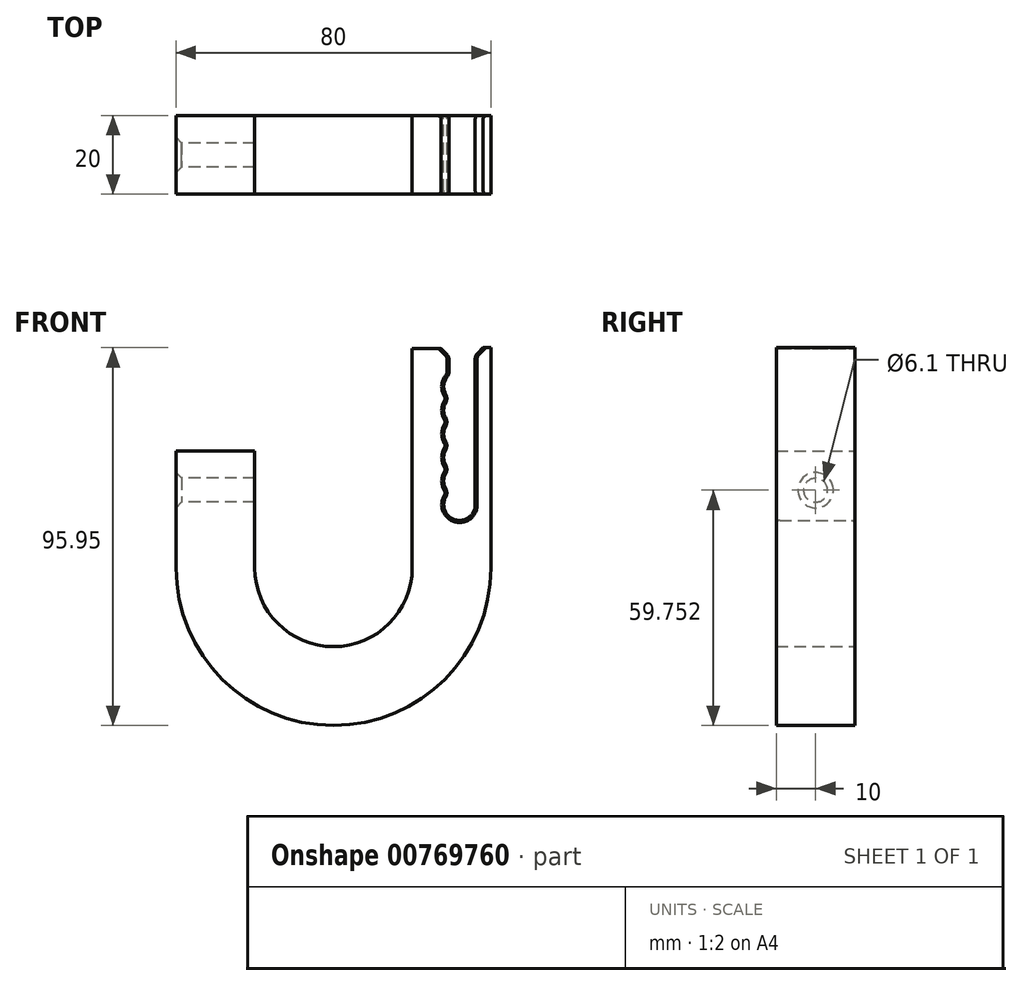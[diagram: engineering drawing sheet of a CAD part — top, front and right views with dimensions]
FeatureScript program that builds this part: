
annotation { "Feature Type Name" : "Feature", "Feature Type Description" : "" }
export const myFeature = defineFeature(function(context is Context, id is Id, definition is map)
    precondition{}
    {
        {
            var Q0;
            Q0=qCreatedBy(makeId("Front.planeOp"),FACE);
            var sketch = newSketch(context, id + "F0", { "sketchPlane" : qUnion([Q0])});
            skArc(sketch, "E0", {"start": v(0.07, 3) * mm, "mid": v(1.07, -3.65) * mm, "end": v(6.72, 0) * mm});
            skArc(sketch, "E1", {"start": v(0.07, 9) * mm, "mid": v(-1.28, 6) * mm, "end": v(0.07, 3) * mm});
            skArc(sketch, "E2", {"start": v(0.07, 15) * mm, "mid": v(-1.28, 12) * mm, "end": v(0.07, 9) * mm});
            skArc(sketch, "E3", {"start": v(0.07, 21) * mm, "mid": v(-1.28, 18) * mm, "end": v(0.07, 15) * mm});
            skArc(sketch, "E4", {"start": v(0.07, 27) * mm, "mid": v(-1.28, 24) * mm, "end": v(0.07, 21) * mm});
            skArc(sketch, "E5", {"start": v(0.07, 33) * mm, "mid": v(-1.28, 30) * mm, "end": v(0.07, 27) * mm});
            skLineSegment(sketch, "E6", {"start": v(6.72, 30) * mm, "end": v(6.72, 0) * mm});
            skLineSegment(sketch, "E7", {"start": v(0.07, 39.67) * mm, "end": v(-9.28, 39.67) * mm});
            skLineSegment(sketch, "E8", {"start": v(-9.28, 39.67) * mm, "end": v(-9.28, -16.06) * mm});
            skLineSegment(sketch, "E9", {"start": v(10.72, -16.06) * mm, "end": v(10.72, 39.9) * mm});
            skLineSegment(sketch, "E10", {"start": v(10.72, 39.9) * mm, "end": v(6.72, 39.9) * mm});
            skLineSegment(sketch, "E11", {"start": v(6.72, 39.9) * mm, "end": v(6.72, 30) * mm});
            skLineSegment(sketch, "E12", {"start": v(0.07, 33) * mm, "end": v(0.07, 39.67) * mm});
            skArc(sketch, "E13", {"start": v(-9.28, -16.06) * mm, "mid": v(-29.28, -36.06) * mm, "end": v(-49.28, -16.06) * mm});
            skArc(sketch, "E14", {"start": v(10.72, -16.06) * mm, "mid": v(-29.28, -56.06) * mm, "end": v(-69.28, -16.06) * mm});
            skLineSegment(sketch, "E15", {"start": v(-69.28, -16.06) * mm, "end": v(-69.28, 13.7) * mm});
            skLineSegment(sketch, "E16", {"start": v(-69.28, 13.7) * mm, "end": v(-49.28, 13.7) * mm});
            skLineSegment(sketch, "E17", {"start": v(-49.28, 13.7) * mm, "end": v(-49.28, -16.06) * mm});
            skSolve(sketch);
        }
        {
            var Q0;
            Q0 = qSketchRegion(id + "F0", true);
            extrude(context, id + "F1", {"entities" : qUnion([Q0]), "endBound" : BoundingType.SYMMETRIC, "depth" : 20 * mm, "offsetDistance" : 25 * mm});
        }
        {
            var Q0;
            Q0=makeQuery(id+"F1.opExtrude","SWEPT_EDGE",EDGE,{"disambiguationData":[OSD([sQuery(id+"F0.wireOp",EDGE,"E7"),sQuery(id+"F0.wireOp",EDGE,"E12")])]});
            var Q1;
            Q1=makeQuery(id+"F1.opExtrude","SWEPT_EDGE",EDGE,{"disambiguationData":[OSD([sQuery(id+"F0.wireOp",EDGE,"E10"),sQuery(id+"F0.wireOp",EDGE,"E11")])]});
            chamfer(context, id + "F2", {"entities" : qUnion([Q0, Q1]), "width" : 2 * mm, "tangentPropagation" : true});
        }
        {
            var Q0;
            {var subQ0=sQuery(id+"F0.wireOp",EDGE,"E12");Q0=makeQuery(id+"F2.opChamfer","BLEND_EDGE",EDGE,{"blendedFrom":[makeQuery(id+"F1.opExtrude","SWEPT_EDGE",EDGE,{"disambiguationData":[OSD([sQuery(id+"F0.wireOp",EDGE,"E7"),subQ0])]}),makeQuery(id+"F1.opExtrude","SWEPT_FACE",FACE,{"disambiguationData":[OSD([subQ0])]})],"blendedInto":[makeQuery(id+"F1.opExtrude","SWEPT_FACE",FACE,{"disambiguationData":[OSD([subQ0])]})]});}
            var Q1;
            Q1=makeQuery(id+"F1.opExtrude","SWEPT_EDGE",EDGE,{"disambiguationData":[OSD([sQuery(id+"F0.wireOp",EDGE,"E5"),sQuery(id+"F0.wireOp",EDGE,"E12")])]});
            var Q2;
            Q2=makeQuery(id+"F1.opExtrude","SWEPT_EDGE",EDGE,{"disambiguationData":[OSD([sQuery(id+"F0.wireOp",EDGE,"E4"),sQuery(id+"F0.wireOp",EDGE,"E5")])]});
            var Q3;
            Q3=makeQuery(id+"F1.opExtrude","SWEPT_EDGE",EDGE,{"disambiguationData":[OSD([sQuery(id+"F0.wireOp",EDGE,"E3"),sQuery(id+"F0.wireOp",EDGE,"E4")])]});
            var Q4;
            Q4=makeQuery(id+"F1.opExtrude","SWEPT_EDGE",EDGE,{"disambiguationData":[OSD([sQuery(id+"F0.wireOp",EDGE,"E2"),sQuery(id+"F0.wireOp",EDGE,"E3")])]});
            var Q5;
            Q5=makeQuery(id+"F1.opExtrude","SWEPT_EDGE",EDGE,{"disambiguationData":[OSD([sQuery(id+"F0.wireOp",EDGE,"E1"),sQuery(id+"F0.wireOp",EDGE,"E2")])]});
            var Q6;
            Q6=makeQuery(id+"F1.opExtrude","SWEPT_EDGE",EDGE,{"disambiguationData":[OSD([sQuery(id+"F0.wireOp",EDGE,"E0"),sQuery(id+"F0.wireOp",EDGE,"E1")])]});
            var Q7;
            {var subQ0=sQuery(id+"F0.wireOp",EDGE,"E11");Q7=makeQuery(id+"F2.opChamfer","BLEND_EDGE",EDGE,{"blendedFrom":[makeQuery(id+"F1.opExtrude","SWEPT_EDGE",EDGE,{"disambiguationData":[OSD([sQuery(id+"F0.wireOp",EDGE,"E10"),subQ0])]}),makeQuery(id+"F1.opExtrude","SWEPT_FACE",FACE,{"disambiguationData":[OSD([sQuery(id+"F0.wireOp",EDGE,"E6"),subQ0])]})],"blendedInto":[makeQuery(id+"F1.opExtrude","SWEPT_FACE",FACE,{"disambiguationData":[OSD([sQuery(id+"F0.wireOp",EDGE,"E6"),subQ0])]})]});}
            fillet(context, id + "F3", {"entities" : qUnion([Q0, Q1, Q2, Q3, Q4, Q5, Q6, Q7]), "radius" : 2 * mm, "tangentPropagation" : true, "allowEdgeOverflow" : false});
        }
        {
            var Q0;
            Q0=makeQuery(id+"F1.opExtrude","CAP_EDGE",EDGE,{"disambiguationData":[OSD([sQuery(id+"F0.wireOp",EDGE,"E5")])],"isStart":false});
            var Q1;
            {var subQ0=sQuery(id+"F0.wireOp",EDGE,"E5");var subQ1=sQuery(id+"F0.wireOp",EDGE,"E4");Q1=makeQuery(id+"F3.opFillet","BLEND_EDGE",EDGE,{"blendedFrom":[makeQuery(id+"F1.opExtrude","SWEPT_EDGE",EDGE,{"disambiguationData":[OSD([subQ1,subQ0])]}),makeQuery(id+"F1.opExtrude","CAP_FACE",FACE,{"disambiguationData":[OSD([sQuery(id+"F0.wireOp",EDGE,"E0"),sQuery(id+"F0.wireOp",EDGE,"E1"),sQuery(id+"F0.wireOp",EDGE,"E2"),sQuery(id+"F0.wireOp",EDGE,"E3"),subQ1,subQ0,sQuery(id+"F0.wireOp",EDGE,"E6"),sQuery(id+"F0.wireOp",EDGE,"E7"),sQuery(id+"F0.wireOp",EDGE,"E8"),sQuery(id+"F0.wireOp",EDGE,"E9"),sQuery(id+"F0.wireOp",EDGE,"E10"),sQuery(id+"F0.wireOp",EDGE,"E11"),sQuery(id+"F0.wireOp",EDGE,"E12"),sQuery(id+"F0.wireOp",EDGE,"E13"),sQuery(id+"F0.wireOp",EDGE,"E14"),sQuery(id+"F0.wireOp",EDGE,"E15"),sQuery(id+"F0.wireOp",EDGE,"E16"),sQuery(id+"F0.wireOp",EDGE,"E17")])],"isStart":false})],"blendedInto":[makeQuery(id+"F1.opExtrude","CAP_FACE",FACE,{"disambiguationData":[OSD([sQuery(id+"F0.wireOp",EDGE,"E0"),sQuery(id+"F0.wireOp",EDGE,"E1"),sQuery(id+"F0.wireOp",EDGE,"E2"),sQuery(id+"F0.wireOp",EDGE,"E3"),subQ1,subQ0,sQuery(id+"F0.wireOp",EDGE,"E6"),sQuery(id+"F0.wireOp",EDGE,"E7"),sQuery(id+"F0.wireOp",EDGE,"E8"),sQuery(id+"F0.wireOp",EDGE,"E9"),sQuery(id+"F0.wireOp",EDGE,"E10"),sQuery(id+"F0.wireOp",EDGE,"E11"),sQuery(id+"F0.wireOp",EDGE,"E12"),sQuery(id+"F0.wireOp",EDGE,"E13"),sQuery(id+"F0.wireOp",EDGE,"E14"),sQuery(id+"F0.wireOp",EDGE,"E15"),sQuery(id+"F0.wireOp",EDGE,"E16"),sQuery(id+"F0.wireOp",EDGE,"E17")])],"isStart":false})]});}
            var Q2;
            Q2=makeQuery(id+"F1.opExtrude","CAP_EDGE",EDGE,{"disambiguationData":[OSD([sQuery(id+"F0.wireOp",EDGE,"E4")])],"isStart":false});
            var Q3;
            {var subQ0=sQuery(id+"F0.wireOp",EDGE,"E4");var subQ1=sQuery(id+"F0.wireOp",EDGE,"E3");Q3=makeQuery(id+"F3.opFillet","BLEND_EDGE",EDGE,{"blendedFrom":[makeQuery(id+"F1.opExtrude","SWEPT_EDGE",EDGE,{"disambiguationData":[OSD([subQ1,subQ0])]}),makeQuery(id+"F1.opExtrude","CAP_FACE",FACE,{"disambiguationData":[OSD([sQuery(id+"F0.wireOp",EDGE,"E0"),sQuery(id+"F0.wireOp",EDGE,"E1"),sQuery(id+"F0.wireOp",EDGE,"E2"),subQ1,subQ0,sQuery(id+"F0.wireOp",EDGE,"E5"),sQuery(id+"F0.wireOp",EDGE,"E6"),sQuery(id+"F0.wireOp",EDGE,"E7"),sQuery(id+"F0.wireOp",EDGE,"E8"),sQuery(id+"F0.wireOp",EDGE,"E9"),sQuery(id+"F0.wireOp",EDGE,"E10"),sQuery(id+"F0.wireOp",EDGE,"E11"),sQuery(id+"F0.wireOp",EDGE,"E12"),sQuery(id+"F0.wireOp",EDGE,"E13"),sQuery(id+"F0.wireOp",EDGE,"E14"),sQuery(id+"F0.wireOp",EDGE,"E15"),sQuery(id+"F0.wireOp",EDGE,"E16"),sQuery(id+"F0.wireOp",EDGE,"E17")])],"isStart":false})],"blendedInto":[makeQuery(id+"F1.opExtrude","CAP_FACE",FACE,{"disambiguationData":[OSD([sQuery(id+"F0.wireOp",EDGE,"E0"),sQuery(id+"F0.wireOp",EDGE,"E1"),sQuery(id+"F0.wireOp",EDGE,"E2"),subQ1,subQ0,sQuery(id+"F0.wireOp",EDGE,"E5"),sQuery(id+"F0.wireOp",EDGE,"E6"),sQuery(id+"F0.wireOp",EDGE,"E7"),sQuery(id+"F0.wireOp",EDGE,"E8"),sQuery(id+"F0.wireOp",EDGE,"E9"),sQuery(id+"F0.wireOp",EDGE,"E10"),sQuery(id+"F0.wireOp",EDGE,"E11"),sQuery(id+"F0.wireOp",EDGE,"E12"),sQuery(id+"F0.wireOp",EDGE,"E13"),sQuery(id+"F0.wireOp",EDGE,"E14"),sQuery(id+"F0.wireOp",EDGE,"E15"),sQuery(id+"F0.wireOp",EDGE,"E16"),sQuery(id+"F0.wireOp",EDGE,"E17")])],"isStart":false})]});}
            var Q4;
            Q4=makeQuery(id+"F1.opExtrude","CAP_EDGE",EDGE,{"disambiguationData":[OSD([sQuery(id+"F0.wireOp",EDGE,"E3")])],"isStart":false});
            var Q5;
            {var subQ0=sQuery(id+"F0.wireOp",EDGE,"E3");var subQ1=sQuery(id+"F0.wireOp",EDGE,"E2");Q5=makeQuery(id+"F3.opFillet","BLEND_EDGE",EDGE,{"blendedFrom":[makeQuery(id+"F1.opExtrude","SWEPT_EDGE",EDGE,{"disambiguationData":[OSD([subQ1,subQ0])]}),makeQuery(id+"F1.opExtrude","CAP_FACE",FACE,{"disambiguationData":[OSD([sQuery(id+"F0.wireOp",EDGE,"E0"),sQuery(id+"F0.wireOp",EDGE,"E1"),subQ1,subQ0,sQuery(id+"F0.wireOp",EDGE,"E4"),sQuery(id+"F0.wireOp",EDGE,"E5"),sQuery(id+"F0.wireOp",EDGE,"E6"),sQuery(id+"F0.wireOp",EDGE,"E7"),sQuery(id+"F0.wireOp",EDGE,"E8"),sQuery(id+"F0.wireOp",EDGE,"E9"),sQuery(id+"F0.wireOp",EDGE,"E10"),sQuery(id+"F0.wireOp",EDGE,"E11"),sQuery(id+"F0.wireOp",EDGE,"E12"),sQuery(id+"F0.wireOp",EDGE,"E13"),sQuery(id+"F0.wireOp",EDGE,"E14"),sQuery(id+"F0.wireOp",EDGE,"E15"),sQuery(id+"F0.wireOp",EDGE,"E16"),sQuery(id+"F0.wireOp",EDGE,"E17")])],"isStart":false})],"blendedInto":[makeQuery(id+"F1.opExtrude","CAP_FACE",FACE,{"disambiguationData":[OSD([sQuery(id+"F0.wireOp",EDGE,"E0"),sQuery(id+"F0.wireOp",EDGE,"E1"),subQ1,subQ0,sQuery(id+"F0.wireOp",EDGE,"E4"),sQuery(id+"F0.wireOp",EDGE,"E5"),sQuery(id+"F0.wireOp",EDGE,"E6"),sQuery(id+"F0.wireOp",EDGE,"E7"),sQuery(id+"F0.wireOp",EDGE,"E8"),sQuery(id+"F0.wireOp",EDGE,"E9"),sQuery(id+"F0.wireOp",EDGE,"E10"),sQuery(id+"F0.wireOp",EDGE,"E11"),sQuery(id+"F0.wireOp",EDGE,"E12"),sQuery(id+"F0.wireOp",EDGE,"E13"),sQuery(id+"F0.wireOp",EDGE,"E14"),sQuery(id+"F0.wireOp",EDGE,"E15"),sQuery(id+"F0.wireOp",EDGE,"E16"),sQuery(id+"F0.wireOp",EDGE,"E17")])],"isStart":false})]});}
            var Q6;
            Q6=makeQuery(id+"F1.opExtrude","CAP_EDGE",EDGE,{"disambiguationData":[OSD([sQuery(id+"F0.wireOp",EDGE,"E2")])],"isStart":false});
            var Q7;
            {var subQ0=sQuery(id+"F0.wireOp",EDGE,"E2");var subQ1=sQuery(id+"F0.wireOp",EDGE,"E1");Q7=makeQuery(id+"F3.opFillet","BLEND_EDGE",EDGE,{"blendedFrom":[makeQuery(id+"F1.opExtrude","SWEPT_EDGE",EDGE,{"disambiguationData":[OSD([subQ1,subQ0])]}),makeQuery(id+"F1.opExtrude","CAP_FACE",FACE,{"disambiguationData":[OSD([sQuery(id+"F0.wireOp",EDGE,"E0"),subQ1,subQ0,sQuery(id+"F0.wireOp",EDGE,"E3"),sQuery(id+"F0.wireOp",EDGE,"E4"),sQuery(id+"F0.wireOp",EDGE,"E5"),sQuery(id+"F0.wireOp",EDGE,"E6"),sQuery(id+"F0.wireOp",EDGE,"E7"),sQuery(id+"F0.wireOp",EDGE,"E8"),sQuery(id+"F0.wireOp",EDGE,"E9"),sQuery(id+"F0.wireOp",EDGE,"E10"),sQuery(id+"F0.wireOp",EDGE,"E11"),sQuery(id+"F0.wireOp",EDGE,"E12"),sQuery(id+"F0.wireOp",EDGE,"E13"),sQuery(id+"F0.wireOp",EDGE,"E14"),sQuery(id+"F0.wireOp",EDGE,"E15"),sQuery(id+"F0.wireOp",EDGE,"E16"),sQuery(id+"F0.wireOp",EDGE,"E17")])],"isStart":false})],"blendedInto":[makeQuery(id+"F1.opExtrude","CAP_FACE",FACE,{"disambiguationData":[OSD([sQuery(id+"F0.wireOp",EDGE,"E0"),subQ1,subQ0,sQuery(id+"F0.wireOp",EDGE,"E3"),sQuery(id+"F0.wireOp",EDGE,"E4"),sQuery(id+"F0.wireOp",EDGE,"E5"),sQuery(id+"F0.wireOp",EDGE,"E6"),sQuery(id+"F0.wireOp",EDGE,"E7"),sQuery(id+"F0.wireOp",EDGE,"E8"),sQuery(id+"F0.wireOp",EDGE,"E9"),sQuery(id+"F0.wireOp",EDGE,"E10"),sQuery(id+"F0.wireOp",EDGE,"E11"),sQuery(id+"F0.wireOp",EDGE,"E12"),sQuery(id+"F0.wireOp",EDGE,"E13"),sQuery(id+"F0.wireOp",EDGE,"E14"),sQuery(id+"F0.wireOp",EDGE,"E15"),sQuery(id+"F0.wireOp",EDGE,"E16"),sQuery(id+"F0.wireOp",EDGE,"E17")])],"isStart":false})]});}
            var Q8;
            Q8=makeQuery(id+"F1.opExtrude","CAP_EDGE",EDGE,{"disambiguationData":[OSD([sQuery(id+"F0.wireOp",EDGE,"E1")])],"isStart":false});
            var Q9;
            {var subQ0=sQuery(id+"F0.wireOp",EDGE,"E1");var subQ1=sQuery(id+"F0.wireOp",EDGE,"E0");Q9=makeQuery(id+"F3.opFillet","BLEND_EDGE",EDGE,{"blendedFrom":[makeQuery(id+"F1.opExtrude","SWEPT_EDGE",EDGE,{"disambiguationData":[OSD([subQ1,subQ0])]}),makeQuery(id+"F1.opExtrude","CAP_FACE",FACE,{"disambiguationData":[OSD([subQ1,subQ0,sQuery(id+"F0.wireOp",EDGE,"E2"),sQuery(id+"F0.wireOp",EDGE,"E3"),sQuery(id+"F0.wireOp",EDGE,"E4"),sQuery(id+"F0.wireOp",EDGE,"E5"),sQuery(id+"F0.wireOp",EDGE,"E6"),sQuery(id+"F0.wireOp",EDGE,"E7"),sQuery(id+"F0.wireOp",EDGE,"E8"),sQuery(id+"F0.wireOp",EDGE,"E9"),sQuery(id+"F0.wireOp",EDGE,"E10"),sQuery(id+"F0.wireOp",EDGE,"E11"),sQuery(id+"F0.wireOp",EDGE,"E12"),sQuery(id+"F0.wireOp",EDGE,"E13"),sQuery(id+"F0.wireOp",EDGE,"E14"),sQuery(id+"F0.wireOp",EDGE,"E15"),sQuery(id+"F0.wireOp",EDGE,"E16"),sQuery(id+"F0.wireOp",EDGE,"E17")])],"isStart":false})],"blendedInto":[makeQuery(id+"F1.opExtrude","CAP_FACE",FACE,{"disambiguationData":[OSD([subQ1,subQ0,sQuery(id+"F0.wireOp",EDGE,"E2"),sQuery(id+"F0.wireOp",EDGE,"E3"),sQuery(id+"F0.wireOp",EDGE,"E4"),sQuery(id+"F0.wireOp",EDGE,"E5"),sQuery(id+"F0.wireOp",EDGE,"E6"),sQuery(id+"F0.wireOp",EDGE,"E7"),sQuery(id+"F0.wireOp",EDGE,"E8"),sQuery(id+"F0.wireOp",EDGE,"E9"),sQuery(id+"F0.wireOp",EDGE,"E10"),sQuery(id+"F0.wireOp",EDGE,"E11"),sQuery(id+"F0.wireOp",EDGE,"E12"),sQuery(id+"F0.wireOp",EDGE,"E13"),sQuery(id+"F0.wireOp",EDGE,"E14"),sQuery(id+"F0.wireOp",EDGE,"E15"),sQuery(id+"F0.wireOp",EDGE,"E16"),sQuery(id+"F0.wireOp",EDGE,"E17")])],"isStart":false})]});}
            var Q10;
            {var subQ0=sQuery(id+"F0.wireOp",EDGE,"E12");var subQ1=sQuery(id+"F0.wireOp",EDGE,"E5");Q10=makeQuery(id+"F3.opFillet","BLEND_EDGE",EDGE,{"blendedFrom":[makeQuery(id+"F1.opExtrude","SWEPT_EDGE",EDGE,{"disambiguationData":[OSD([subQ1,subQ0])]}),makeQuery(id+"F1.opExtrude","CAP_FACE",FACE,{"disambiguationData":[OSD([sQuery(id+"F0.wireOp",EDGE,"E0"),sQuery(id+"F0.wireOp",EDGE,"E1"),sQuery(id+"F0.wireOp",EDGE,"E2"),sQuery(id+"F0.wireOp",EDGE,"E3"),sQuery(id+"F0.wireOp",EDGE,"E4"),subQ1,sQuery(id+"F0.wireOp",EDGE,"E6"),sQuery(id+"F0.wireOp",EDGE,"E7"),sQuery(id+"F0.wireOp",EDGE,"E8"),sQuery(id+"F0.wireOp",EDGE,"E9"),sQuery(id+"F0.wireOp",EDGE,"E10"),sQuery(id+"F0.wireOp",EDGE,"E11"),subQ0,sQuery(id+"F0.wireOp",EDGE,"E13"),sQuery(id+"F0.wireOp",EDGE,"E14"),sQuery(id+"F0.wireOp",EDGE,"E15"),sQuery(id+"F0.wireOp",EDGE,"E16"),sQuery(id+"F0.wireOp",EDGE,"E17")])],"isStart":false})],"blendedInto":[makeQuery(id+"F1.opExtrude","CAP_FACE",FACE,{"disambiguationData":[OSD([sQuery(id+"F0.wireOp",EDGE,"E0"),sQuery(id+"F0.wireOp",EDGE,"E1"),sQuery(id+"F0.wireOp",EDGE,"E2"),sQuery(id+"F0.wireOp",EDGE,"E3"),sQuery(id+"F0.wireOp",EDGE,"E4"),subQ1,sQuery(id+"F0.wireOp",EDGE,"E6"),sQuery(id+"F0.wireOp",EDGE,"E7"),sQuery(id+"F0.wireOp",EDGE,"E8"),sQuery(id+"F0.wireOp",EDGE,"E9"),sQuery(id+"F0.wireOp",EDGE,"E10"),sQuery(id+"F0.wireOp",EDGE,"E11"),subQ0,sQuery(id+"F0.wireOp",EDGE,"E13"),sQuery(id+"F0.wireOp",EDGE,"E14"),sQuery(id+"F0.wireOp",EDGE,"E15"),sQuery(id+"F0.wireOp",EDGE,"E16"),sQuery(id+"F0.wireOp",EDGE,"E17")])],"isStart":false})]});}
            var Q11;
            Q11=makeQuery(id+"F1.opExtrude","CAP_EDGE",EDGE,{"disambiguationData":[OSD([sQuery(id+"F0.wireOp",EDGE,"E12")])],"isStart":false});
            var Q12;
            {var subQ0=sQuery(id+"F0.wireOp",EDGE,"E12");var subQ1=sQuery(id+"F0.wireOp",EDGE,"E7");Q12=makeQuery(id+"F3.opFillet","BLEND_EDGE",EDGE,{"blendedFrom":[makeQuery(id+"F2.opChamfer","BLEND_EDGE",EDGE,{"blendedFrom":[makeQuery(id+"F1.opExtrude","SWEPT_EDGE",EDGE,{"disambiguationData":[OSD([subQ1,subQ0])]}),makeQuery(id+"F1.opExtrude","SWEPT_FACE",FACE,{"disambiguationData":[OSD([subQ0])]})],"blendedInto":[makeQuery(id+"F1.opExtrude","SWEPT_FACE",FACE,{"disambiguationData":[OSD([subQ0])]})]}),makeQuery(id+"F1.opExtrude","CAP_FACE",FACE,{"disambiguationData":[OSD([sQuery(id+"F0.wireOp",EDGE,"E0"),sQuery(id+"F0.wireOp",EDGE,"E1"),sQuery(id+"F0.wireOp",EDGE,"E2"),sQuery(id+"F0.wireOp",EDGE,"E3"),sQuery(id+"F0.wireOp",EDGE,"E4"),sQuery(id+"F0.wireOp",EDGE,"E5"),sQuery(id+"F0.wireOp",EDGE,"E6"),subQ1,sQuery(id+"F0.wireOp",EDGE,"E8"),sQuery(id+"F0.wireOp",EDGE,"E9"),sQuery(id+"F0.wireOp",EDGE,"E10"),sQuery(id+"F0.wireOp",EDGE,"E11"),subQ0,sQuery(id+"F0.wireOp",EDGE,"E13"),sQuery(id+"F0.wireOp",EDGE,"E14"),sQuery(id+"F0.wireOp",EDGE,"E15"),sQuery(id+"F0.wireOp",EDGE,"E16"),sQuery(id+"F0.wireOp",EDGE,"E17")])],"isStart":false})],"blendedInto":[makeQuery(id+"F1.opExtrude","CAP_FACE",FACE,{"disambiguationData":[OSD([sQuery(id+"F0.wireOp",EDGE,"E0"),sQuery(id+"F0.wireOp",EDGE,"E1"),sQuery(id+"F0.wireOp",EDGE,"E2"),sQuery(id+"F0.wireOp",EDGE,"E3"),sQuery(id+"F0.wireOp",EDGE,"E4"),sQuery(id+"F0.wireOp",EDGE,"E5"),sQuery(id+"F0.wireOp",EDGE,"E6"),subQ1,sQuery(id+"F0.wireOp",EDGE,"E8"),sQuery(id+"F0.wireOp",EDGE,"E9"),sQuery(id+"F0.wireOp",EDGE,"E10"),sQuery(id+"F0.wireOp",EDGE,"E11"),subQ0,sQuery(id+"F0.wireOp",EDGE,"E13"),sQuery(id+"F0.wireOp",EDGE,"E14"),sQuery(id+"F0.wireOp",EDGE,"E15"),sQuery(id+"F0.wireOp",EDGE,"E16"),sQuery(id+"F0.wireOp",EDGE,"E17")])],"isStart":false})]});}
            var Q13;
            {var subQ0=sQuery(id+"F0.wireOp",EDGE,"E12");var subQ1=sQuery(id+"F0.wireOp",EDGE,"E7");Q13=makeQuery(id+"F2.opChamfer","BLEND_EDGE",EDGE,{"blendedFrom":[makeQuery(id+"F1.opExtrude","SWEPT_EDGE",EDGE,{"disambiguationData":[OSD([subQ1,subQ0])]}),makeQuery(id+"F1.opExtrude","CAP_FACE",FACE,{"disambiguationData":[OSD([sQuery(id+"F0.wireOp",EDGE,"E0"),sQuery(id+"F0.wireOp",EDGE,"E1"),sQuery(id+"F0.wireOp",EDGE,"E2"),sQuery(id+"F0.wireOp",EDGE,"E3"),sQuery(id+"F0.wireOp",EDGE,"E4"),sQuery(id+"F0.wireOp",EDGE,"E5"),sQuery(id+"F0.wireOp",EDGE,"E6"),subQ1,sQuery(id+"F0.wireOp",EDGE,"E8"),sQuery(id+"F0.wireOp",EDGE,"E9"),sQuery(id+"F0.wireOp",EDGE,"E10"),sQuery(id+"F0.wireOp",EDGE,"E11"),subQ0,sQuery(id+"F0.wireOp",EDGE,"E13"),sQuery(id+"F0.wireOp",EDGE,"E14"),sQuery(id+"F0.wireOp",EDGE,"E15"),sQuery(id+"F0.wireOp",EDGE,"E16"),sQuery(id+"F0.wireOp",EDGE,"E17")])],"isStart":false})],"blendedInto":[makeQuery(id+"F1.opExtrude","CAP_FACE",FACE,{"disambiguationData":[OSD([sQuery(id+"F0.wireOp",EDGE,"E0"),sQuery(id+"F0.wireOp",EDGE,"E1"),sQuery(id+"F0.wireOp",EDGE,"E2"),sQuery(id+"F0.wireOp",EDGE,"E3"),sQuery(id+"F0.wireOp",EDGE,"E4"),sQuery(id+"F0.wireOp",EDGE,"E5"),sQuery(id+"F0.wireOp",EDGE,"E6"),subQ1,sQuery(id+"F0.wireOp",EDGE,"E8"),sQuery(id+"F0.wireOp",EDGE,"E9"),sQuery(id+"F0.wireOp",EDGE,"E10"),sQuery(id+"F0.wireOp",EDGE,"E11"),subQ0,sQuery(id+"F0.wireOp",EDGE,"E13"),sQuery(id+"F0.wireOp",EDGE,"E14"),sQuery(id+"F0.wireOp",EDGE,"E15"),sQuery(id+"F0.wireOp",EDGE,"E16"),sQuery(id+"F0.wireOp",EDGE,"E17")])],"isStart":false})]});}
            var Q14;
            Q14=makeQuery(id+"F1.opExtrude","CAP_EDGE",EDGE,{"disambiguationData":[OSD([sQuery(id+"F0.wireOp",EDGE,"E0")])],"isStart":false});
            var Q15;
            Q15=makeQuery(id+"F1.opExtrude","CAP_EDGE",EDGE,{"disambiguationData":[OSD([sQuery(id+"F0.wireOp",EDGE,"E6"),sQuery(id+"F0.wireOp",EDGE,"E11")])],"isStart":false});
            var Q16;
            {var subQ0=sQuery(id+"F0.wireOp",EDGE,"E11");var subQ1=sQuery(id+"F0.wireOp",EDGE,"E10");var subQ2=sQuery(id+"F0.wireOp",EDGE,"E6");Q16=makeQuery(id+"F3.opFillet","BLEND_EDGE",EDGE,{"blendedFrom":[makeQuery(id+"F2.opChamfer","BLEND_EDGE",EDGE,{"blendedFrom":[makeQuery(id+"F1.opExtrude","SWEPT_EDGE",EDGE,{"disambiguationData":[OSD([subQ1,subQ0])]}),makeQuery(id+"F1.opExtrude","SWEPT_FACE",FACE,{"disambiguationData":[OSD([subQ2,subQ0])]})],"blendedInto":[makeQuery(id+"F1.opExtrude","SWEPT_FACE",FACE,{"disambiguationData":[OSD([subQ2,subQ0])]})]}),makeQuery(id+"F1.opExtrude","CAP_FACE",FACE,{"disambiguationData":[OSD([sQuery(id+"F0.wireOp",EDGE,"E0"),sQuery(id+"F0.wireOp",EDGE,"E1"),sQuery(id+"F0.wireOp",EDGE,"E2"),sQuery(id+"F0.wireOp",EDGE,"E3"),sQuery(id+"F0.wireOp",EDGE,"E4"),sQuery(id+"F0.wireOp",EDGE,"E5"),subQ2,sQuery(id+"F0.wireOp",EDGE,"E7"),sQuery(id+"F0.wireOp",EDGE,"E8"),sQuery(id+"F0.wireOp",EDGE,"E9"),subQ1,subQ0,sQuery(id+"F0.wireOp",EDGE,"E12"),sQuery(id+"F0.wireOp",EDGE,"E13"),sQuery(id+"F0.wireOp",EDGE,"E14"),sQuery(id+"F0.wireOp",EDGE,"E15"),sQuery(id+"F0.wireOp",EDGE,"E16"),sQuery(id+"F0.wireOp",EDGE,"E17")])],"isStart":false})],"blendedInto":[makeQuery(id+"F1.opExtrude","CAP_FACE",FACE,{"disambiguationData":[OSD([sQuery(id+"F0.wireOp",EDGE,"E0"),sQuery(id+"F0.wireOp",EDGE,"E1"),sQuery(id+"F0.wireOp",EDGE,"E2"),sQuery(id+"F0.wireOp",EDGE,"E3"),sQuery(id+"F0.wireOp",EDGE,"E4"),sQuery(id+"F0.wireOp",EDGE,"E5"),subQ2,sQuery(id+"F0.wireOp",EDGE,"E7"),sQuery(id+"F0.wireOp",EDGE,"E8"),sQuery(id+"F0.wireOp",EDGE,"E9"),subQ1,subQ0,sQuery(id+"F0.wireOp",EDGE,"E12"),sQuery(id+"F0.wireOp",EDGE,"E13"),sQuery(id+"F0.wireOp",EDGE,"E14"),sQuery(id+"F0.wireOp",EDGE,"E15"),sQuery(id+"F0.wireOp",EDGE,"E16"),sQuery(id+"F0.wireOp",EDGE,"E17")])],"isStart":false})]});}
            var Q17;
            {var subQ0=sQuery(id+"F0.wireOp",EDGE,"E11");var subQ1=sQuery(id+"F0.wireOp",EDGE,"E10");Q17=makeQuery(id+"F2.opChamfer","BLEND_EDGE",EDGE,{"blendedFrom":[makeQuery(id+"F1.opExtrude","SWEPT_EDGE",EDGE,{"disambiguationData":[OSD([subQ1,subQ0])]}),makeQuery(id+"F1.opExtrude","CAP_FACE",FACE,{"disambiguationData":[OSD([sQuery(id+"F0.wireOp",EDGE,"E0"),sQuery(id+"F0.wireOp",EDGE,"E1"),sQuery(id+"F0.wireOp",EDGE,"E2"),sQuery(id+"F0.wireOp",EDGE,"E3"),sQuery(id+"F0.wireOp",EDGE,"E4"),sQuery(id+"F0.wireOp",EDGE,"E5"),sQuery(id+"F0.wireOp",EDGE,"E6"),sQuery(id+"F0.wireOp",EDGE,"E7"),sQuery(id+"F0.wireOp",EDGE,"E8"),sQuery(id+"F0.wireOp",EDGE,"E9"),subQ1,subQ0,sQuery(id+"F0.wireOp",EDGE,"E12"),sQuery(id+"F0.wireOp",EDGE,"E13"),sQuery(id+"F0.wireOp",EDGE,"E14"),sQuery(id+"F0.wireOp",EDGE,"E15"),sQuery(id+"F0.wireOp",EDGE,"E16"),sQuery(id+"F0.wireOp",EDGE,"E17")])],"isStart":false})],"blendedInto":[makeQuery(id+"F1.opExtrude","CAP_FACE",FACE,{"disambiguationData":[OSD([sQuery(id+"F0.wireOp",EDGE,"E0"),sQuery(id+"F0.wireOp",EDGE,"E1"),sQuery(id+"F0.wireOp",EDGE,"E2"),sQuery(id+"F0.wireOp",EDGE,"E3"),sQuery(id+"F0.wireOp",EDGE,"E4"),sQuery(id+"F0.wireOp",EDGE,"E5"),sQuery(id+"F0.wireOp",EDGE,"E6"),sQuery(id+"F0.wireOp",EDGE,"E7"),sQuery(id+"F0.wireOp",EDGE,"E8"),sQuery(id+"F0.wireOp",EDGE,"E9"),subQ1,subQ0,sQuery(id+"F0.wireOp",EDGE,"E12"),sQuery(id+"F0.wireOp",EDGE,"E13"),sQuery(id+"F0.wireOp",EDGE,"E14"),sQuery(id+"F0.wireOp",EDGE,"E15"),sQuery(id+"F0.wireOp",EDGE,"E16"),sQuery(id+"F0.wireOp",EDGE,"E17")])],"isStart":false})]});}
            var Q18;
            {var subQ0=sQuery(id+"F0.wireOp",EDGE,"E11");var subQ1=sQuery(id+"F0.wireOp",EDGE,"E10");Q18=makeQuery(id+"F2.opChamfer","BLEND_EDGE",EDGE,{"blendedFrom":[makeQuery(id+"F1.opExtrude","SWEPT_EDGE",EDGE,{"disambiguationData":[OSD([subQ1,subQ0])]}),makeQuery(id+"F1.opExtrude","CAP_FACE",FACE,{"disambiguationData":[OSD([sQuery(id+"F0.wireOp",EDGE,"E0"),sQuery(id+"F0.wireOp",EDGE,"E1"),sQuery(id+"F0.wireOp",EDGE,"E2"),sQuery(id+"F0.wireOp",EDGE,"E3"),sQuery(id+"F0.wireOp",EDGE,"E4"),sQuery(id+"F0.wireOp",EDGE,"E5"),sQuery(id+"F0.wireOp",EDGE,"E6"),sQuery(id+"F0.wireOp",EDGE,"E7"),sQuery(id+"F0.wireOp",EDGE,"E8"),sQuery(id+"F0.wireOp",EDGE,"E9"),subQ1,subQ0,sQuery(id+"F0.wireOp",EDGE,"E12"),sQuery(id+"F0.wireOp",EDGE,"E13"),sQuery(id+"F0.wireOp",EDGE,"E14"),sQuery(id+"F0.wireOp",EDGE,"E15"),sQuery(id+"F0.wireOp",EDGE,"E16"),sQuery(id+"F0.wireOp",EDGE,"E17")])],"isStart":true})],"blendedInto":[makeQuery(id+"F1.opExtrude","CAP_FACE",FACE,{"disambiguationData":[OSD([sQuery(id+"F0.wireOp",EDGE,"E0"),sQuery(id+"F0.wireOp",EDGE,"E1"),sQuery(id+"F0.wireOp",EDGE,"E2"),sQuery(id+"F0.wireOp",EDGE,"E3"),sQuery(id+"F0.wireOp",EDGE,"E4"),sQuery(id+"F0.wireOp",EDGE,"E5"),sQuery(id+"F0.wireOp",EDGE,"E6"),sQuery(id+"F0.wireOp",EDGE,"E7"),sQuery(id+"F0.wireOp",EDGE,"E8"),sQuery(id+"F0.wireOp",EDGE,"E9"),subQ1,subQ0,sQuery(id+"F0.wireOp",EDGE,"E12"),sQuery(id+"F0.wireOp",EDGE,"E13"),sQuery(id+"F0.wireOp",EDGE,"E14"),sQuery(id+"F0.wireOp",EDGE,"E15"),sQuery(id+"F0.wireOp",EDGE,"E16"),sQuery(id+"F0.wireOp",EDGE,"E17")])],"isStart":true})]});}
            var Q19;
            {var subQ0=sQuery(id+"F0.wireOp",EDGE,"E11");var subQ1=sQuery(id+"F0.wireOp",EDGE,"E10");var subQ2=sQuery(id+"F0.wireOp",EDGE,"E6");Q19=makeQuery(id+"F3.opFillet","BLEND_EDGE",EDGE,{"blendedFrom":[makeQuery(id+"F2.opChamfer","BLEND_EDGE",EDGE,{"blendedFrom":[makeQuery(id+"F1.opExtrude","SWEPT_EDGE",EDGE,{"disambiguationData":[OSD([subQ1,subQ0])]}),makeQuery(id+"F1.opExtrude","SWEPT_FACE",FACE,{"disambiguationData":[OSD([subQ2,subQ0])]})],"blendedInto":[makeQuery(id+"F1.opExtrude","SWEPT_FACE",FACE,{"disambiguationData":[OSD([subQ2,subQ0])]})]}),makeQuery(id+"F1.opExtrude","CAP_FACE",FACE,{"disambiguationData":[OSD([sQuery(id+"F0.wireOp",EDGE,"E0"),sQuery(id+"F0.wireOp",EDGE,"E1"),sQuery(id+"F0.wireOp",EDGE,"E2"),sQuery(id+"F0.wireOp",EDGE,"E3"),sQuery(id+"F0.wireOp",EDGE,"E4"),sQuery(id+"F0.wireOp",EDGE,"E5"),subQ2,sQuery(id+"F0.wireOp",EDGE,"E7"),sQuery(id+"F0.wireOp",EDGE,"E8"),sQuery(id+"F0.wireOp",EDGE,"E9"),subQ1,subQ0,sQuery(id+"F0.wireOp",EDGE,"E12"),sQuery(id+"F0.wireOp",EDGE,"E13"),sQuery(id+"F0.wireOp",EDGE,"E14"),sQuery(id+"F0.wireOp",EDGE,"E15"),sQuery(id+"F0.wireOp",EDGE,"E16"),sQuery(id+"F0.wireOp",EDGE,"E17")])],"isStart":true})],"blendedInto":[makeQuery(id+"F1.opExtrude","CAP_FACE",FACE,{"disambiguationData":[OSD([sQuery(id+"F0.wireOp",EDGE,"E0"),sQuery(id+"F0.wireOp",EDGE,"E1"),sQuery(id+"F0.wireOp",EDGE,"E2"),sQuery(id+"F0.wireOp",EDGE,"E3"),sQuery(id+"F0.wireOp",EDGE,"E4"),sQuery(id+"F0.wireOp",EDGE,"E5"),subQ2,sQuery(id+"F0.wireOp",EDGE,"E7"),sQuery(id+"F0.wireOp",EDGE,"E8"),sQuery(id+"F0.wireOp",EDGE,"E9"),subQ1,subQ0,sQuery(id+"F0.wireOp",EDGE,"E12"),sQuery(id+"F0.wireOp",EDGE,"E13"),sQuery(id+"F0.wireOp",EDGE,"E14"),sQuery(id+"F0.wireOp",EDGE,"E15"),sQuery(id+"F0.wireOp",EDGE,"E16"),sQuery(id+"F0.wireOp",EDGE,"E17")])],"isStart":true})]});}
            var Q20;
            Q20=makeQuery(id+"F1.opExtrude","CAP_EDGE",EDGE,{"disambiguationData":[OSD([sQuery(id+"F0.wireOp",EDGE,"E6"),sQuery(id+"F0.wireOp",EDGE,"E11")])],"isStart":true});
            var Q21;
            Q21=makeQuery(id+"F1.opExtrude","CAP_EDGE",EDGE,{"disambiguationData":[OSD([sQuery(id+"F0.wireOp",EDGE,"E0")])],"isStart":true});
            var Q22;
            {var subQ0=sQuery(id+"F0.wireOp",EDGE,"E1");var subQ1=sQuery(id+"F0.wireOp",EDGE,"E0");Q22=makeQuery(id+"F3.opFillet","BLEND_EDGE",EDGE,{"blendedFrom":[makeQuery(id+"F1.opExtrude","SWEPT_EDGE",EDGE,{"disambiguationData":[OSD([subQ1,subQ0])]}),makeQuery(id+"F1.opExtrude","CAP_FACE",FACE,{"disambiguationData":[OSD([subQ1,subQ0,sQuery(id+"F0.wireOp",EDGE,"E2"),sQuery(id+"F0.wireOp",EDGE,"E3"),sQuery(id+"F0.wireOp",EDGE,"E4"),sQuery(id+"F0.wireOp",EDGE,"E5"),sQuery(id+"F0.wireOp",EDGE,"E6"),sQuery(id+"F0.wireOp",EDGE,"E7"),sQuery(id+"F0.wireOp",EDGE,"E8"),sQuery(id+"F0.wireOp",EDGE,"E9"),sQuery(id+"F0.wireOp",EDGE,"E10"),sQuery(id+"F0.wireOp",EDGE,"E11"),sQuery(id+"F0.wireOp",EDGE,"E12"),sQuery(id+"F0.wireOp",EDGE,"E13"),sQuery(id+"F0.wireOp",EDGE,"E14"),sQuery(id+"F0.wireOp",EDGE,"E15"),sQuery(id+"F0.wireOp",EDGE,"E16"),sQuery(id+"F0.wireOp",EDGE,"E17")])],"isStart":true})],"blendedInto":[makeQuery(id+"F1.opExtrude","CAP_FACE",FACE,{"disambiguationData":[OSD([subQ1,subQ0,sQuery(id+"F0.wireOp",EDGE,"E2"),sQuery(id+"F0.wireOp",EDGE,"E3"),sQuery(id+"F0.wireOp",EDGE,"E4"),sQuery(id+"F0.wireOp",EDGE,"E5"),sQuery(id+"F0.wireOp",EDGE,"E6"),sQuery(id+"F0.wireOp",EDGE,"E7"),sQuery(id+"F0.wireOp",EDGE,"E8"),sQuery(id+"F0.wireOp",EDGE,"E9"),sQuery(id+"F0.wireOp",EDGE,"E10"),sQuery(id+"F0.wireOp",EDGE,"E11"),sQuery(id+"F0.wireOp",EDGE,"E12"),sQuery(id+"F0.wireOp",EDGE,"E13"),sQuery(id+"F0.wireOp",EDGE,"E14"),sQuery(id+"F0.wireOp",EDGE,"E15"),sQuery(id+"F0.wireOp",EDGE,"E16"),sQuery(id+"F0.wireOp",EDGE,"E17")])],"isStart":true})]});}
            var Q23;
            Q23=makeQuery(id+"F1.opExtrude","CAP_EDGE",EDGE,{"disambiguationData":[OSD([sQuery(id+"F0.wireOp",EDGE,"E1")])],"isStart":true});
            var Q24;
            Q24=makeQuery(id+"F1.opExtrude","CAP_EDGE",EDGE,{"disambiguationData":[OSD([sQuery(id+"F0.wireOp",EDGE,"E2")])],"isStart":true});
            var Q25;
            Q25=makeQuery(id+"F1.opExtrude","CAP_EDGE",EDGE,{"disambiguationData":[OSD([sQuery(id+"F0.wireOp",EDGE,"E3")])],"isStart":true});
            var Q26;
            Q26=makeQuery(id+"F1.opExtrude","CAP_EDGE",EDGE,{"disambiguationData":[OSD([sQuery(id+"F0.wireOp",EDGE,"E4")])],"isStart":true});
            var Q27;
            Q27=makeQuery(id+"F1.opExtrude","CAP_EDGE",EDGE,{"disambiguationData":[OSD([sQuery(id+"F0.wireOp",EDGE,"E5")])],"isStart":true});
            var Q28;
            {var subQ0=sQuery(id+"F0.wireOp",EDGE,"E2");var subQ1=sQuery(id+"F0.wireOp",EDGE,"E1");Q28=makeQuery(id+"F3.opFillet","BLEND_EDGE",EDGE,{"blendedFrom":[makeQuery(id+"F1.opExtrude","SWEPT_EDGE",EDGE,{"disambiguationData":[OSD([subQ1,subQ0])]}),makeQuery(id+"F1.opExtrude","CAP_FACE",FACE,{"disambiguationData":[OSD([sQuery(id+"F0.wireOp",EDGE,"E0"),subQ1,subQ0,sQuery(id+"F0.wireOp",EDGE,"E3"),sQuery(id+"F0.wireOp",EDGE,"E4"),sQuery(id+"F0.wireOp",EDGE,"E5"),sQuery(id+"F0.wireOp",EDGE,"E6"),sQuery(id+"F0.wireOp",EDGE,"E7"),sQuery(id+"F0.wireOp",EDGE,"E8"),sQuery(id+"F0.wireOp",EDGE,"E9"),sQuery(id+"F0.wireOp",EDGE,"E10"),sQuery(id+"F0.wireOp",EDGE,"E11"),sQuery(id+"F0.wireOp",EDGE,"E12"),sQuery(id+"F0.wireOp",EDGE,"E13"),sQuery(id+"F0.wireOp",EDGE,"E14"),sQuery(id+"F0.wireOp",EDGE,"E15"),sQuery(id+"F0.wireOp",EDGE,"E16"),sQuery(id+"F0.wireOp",EDGE,"E17")])],"isStart":true})],"blendedInto":[makeQuery(id+"F1.opExtrude","CAP_FACE",FACE,{"disambiguationData":[OSD([sQuery(id+"F0.wireOp",EDGE,"E0"),subQ1,subQ0,sQuery(id+"F0.wireOp",EDGE,"E3"),sQuery(id+"F0.wireOp",EDGE,"E4"),sQuery(id+"F0.wireOp",EDGE,"E5"),sQuery(id+"F0.wireOp",EDGE,"E6"),sQuery(id+"F0.wireOp",EDGE,"E7"),sQuery(id+"F0.wireOp",EDGE,"E8"),sQuery(id+"F0.wireOp",EDGE,"E9"),sQuery(id+"F0.wireOp",EDGE,"E10"),sQuery(id+"F0.wireOp",EDGE,"E11"),sQuery(id+"F0.wireOp",EDGE,"E12"),sQuery(id+"F0.wireOp",EDGE,"E13"),sQuery(id+"F0.wireOp",EDGE,"E14"),sQuery(id+"F0.wireOp",EDGE,"E15"),sQuery(id+"F0.wireOp",EDGE,"E16"),sQuery(id+"F0.wireOp",EDGE,"E17")])],"isStart":true})]});}
            var Q29;
            {var subQ0=sQuery(id+"F0.wireOp",EDGE,"E3");var subQ1=sQuery(id+"F0.wireOp",EDGE,"E2");Q29=makeQuery(id+"F3.opFillet","BLEND_EDGE",EDGE,{"blendedFrom":[makeQuery(id+"F1.opExtrude","SWEPT_EDGE",EDGE,{"disambiguationData":[OSD([subQ1,subQ0])]}),makeQuery(id+"F1.opExtrude","CAP_FACE",FACE,{"disambiguationData":[OSD([sQuery(id+"F0.wireOp",EDGE,"E0"),sQuery(id+"F0.wireOp",EDGE,"E1"),subQ1,subQ0,sQuery(id+"F0.wireOp",EDGE,"E4"),sQuery(id+"F0.wireOp",EDGE,"E5"),sQuery(id+"F0.wireOp",EDGE,"E6"),sQuery(id+"F0.wireOp",EDGE,"E7"),sQuery(id+"F0.wireOp",EDGE,"E8"),sQuery(id+"F0.wireOp",EDGE,"E9"),sQuery(id+"F0.wireOp",EDGE,"E10"),sQuery(id+"F0.wireOp",EDGE,"E11"),sQuery(id+"F0.wireOp",EDGE,"E12"),sQuery(id+"F0.wireOp",EDGE,"E13"),sQuery(id+"F0.wireOp",EDGE,"E14"),sQuery(id+"F0.wireOp",EDGE,"E15"),sQuery(id+"F0.wireOp",EDGE,"E16"),sQuery(id+"F0.wireOp",EDGE,"E17")])],"isStart":true})],"blendedInto":[makeQuery(id+"F1.opExtrude","CAP_FACE",FACE,{"disambiguationData":[OSD([sQuery(id+"F0.wireOp",EDGE,"E0"),sQuery(id+"F0.wireOp",EDGE,"E1"),subQ1,subQ0,sQuery(id+"F0.wireOp",EDGE,"E4"),sQuery(id+"F0.wireOp",EDGE,"E5"),sQuery(id+"F0.wireOp",EDGE,"E6"),sQuery(id+"F0.wireOp",EDGE,"E7"),sQuery(id+"F0.wireOp",EDGE,"E8"),sQuery(id+"F0.wireOp",EDGE,"E9"),sQuery(id+"F0.wireOp",EDGE,"E10"),sQuery(id+"F0.wireOp",EDGE,"E11"),sQuery(id+"F0.wireOp",EDGE,"E12"),sQuery(id+"F0.wireOp",EDGE,"E13"),sQuery(id+"F0.wireOp",EDGE,"E14"),sQuery(id+"F0.wireOp",EDGE,"E15"),sQuery(id+"F0.wireOp",EDGE,"E16"),sQuery(id+"F0.wireOp",EDGE,"E17")])],"isStart":true})]});}
            var Q30;
            {var subQ0=sQuery(id+"F0.wireOp",EDGE,"E4");var subQ1=sQuery(id+"F0.wireOp",EDGE,"E3");Q30=makeQuery(id+"F3.opFillet","BLEND_EDGE",EDGE,{"blendedFrom":[makeQuery(id+"F1.opExtrude","SWEPT_EDGE",EDGE,{"disambiguationData":[OSD([subQ1,subQ0])]}),makeQuery(id+"F1.opExtrude","CAP_FACE",FACE,{"disambiguationData":[OSD([sQuery(id+"F0.wireOp",EDGE,"E0"),sQuery(id+"F0.wireOp",EDGE,"E1"),sQuery(id+"F0.wireOp",EDGE,"E2"),subQ1,subQ0,sQuery(id+"F0.wireOp",EDGE,"E5"),sQuery(id+"F0.wireOp",EDGE,"E6"),sQuery(id+"F0.wireOp",EDGE,"E7"),sQuery(id+"F0.wireOp",EDGE,"E8"),sQuery(id+"F0.wireOp",EDGE,"E9"),sQuery(id+"F0.wireOp",EDGE,"E10"),sQuery(id+"F0.wireOp",EDGE,"E11"),sQuery(id+"F0.wireOp",EDGE,"E12"),sQuery(id+"F0.wireOp",EDGE,"E13"),sQuery(id+"F0.wireOp",EDGE,"E14"),sQuery(id+"F0.wireOp",EDGE,"E15"),sQuery(id+"F0.wireOp",EDGE,"E16"),sQuery(id+"F0.wireOp",EDGE,"E17")])],"isStart":true})],"blendedInto":[makeQuery(id+"F1.opExtrude","CAP_FACE",FACE,{"disambiguationData":[OSD([sQuery(id+"F0.wireOp",EDGE,"E0"),sQuery(id+"F0.wireOp",EDGE,"E1"),sQuery(id+"F0.wireOp",EDGE,"E2"),subQ1,subQ0,sQuery(id+"F0.wireOp",EDGE,"E5"),sQuery(id+"F0.wireOp",EDGE,"E6"),sQuery(id+"F0.wireOp",EDGE,"E7"),sQuery(id+"F0.wireOp",EDGE,"E8"),sQuery(id+"F0.wireOp",EDGE,"E9"),sQuery(id+"F0.wireOp",EDGE,"E10"),sQuery(id+"F0.wireOp",EDGE,"E11"),sQuery(id+"F0.wireOp",EDGE,"E12"),sQuery(id+"F0.wireOp",EDGE,"E13"),sQuery(id+"F0.wireOp",EDGE,"E14"),sQuery(id+"F0.wireOp",EDGE,"E15"),sQuery(id+"F0.wireOp",EDGE,"E16"),sQuery(id+"F0.wireOp",EDGE,"E17")])],"isStart":true})]});}
            var Q31;
            {var subQ0=sQuery(id+"F0.wireOp",EDGE,"E5");var subQ1=sQuery(id+"F0.wireOp",EDGE,"E4");Q31=makeQuery(id+"F3.opFillet","BLEND_EDGE",EDGE,{"blendedFrom":[makeQuery(id+"F1.opExtrude","SWEPT_EDGE",EDGE,{"disambiguationData":[OSD([subQ1,subQ0])]}),makeQuery(id+"F1.opExtrude","CAP_FACE",FACE,{"disambiguationData":[OSD([sQuery(id+"F0.wireOp",EDGE,"E0"),sQuery(id+"F0.wireOp",EDGE,"E1"),sQuery(id+"F0.wireOp",EDGE,"E2"),sQuery(id+"F0.wireOp",EDGE,"E3"),subQ1,subQ0,sQuery(id+"F0.wireOp",EDGE,"E6"),sQuery(id+"F0.wireOp",EDGE,"E7"),sQuery(id+"F0.wireOp",EDGE,"E8"),sQuery(id+"F0.wireOp",EDGE,"E9"),sQuery(id+"F0.wireOp",EDGE,"E10"),sQuery(id+"F0.wireOp",EDGE,"E11"),sQuery(id+"F0.wireOp",EDGE,"E12"),sQuery(id+"F0.wireOp",EDGE,"E13"),sQuery(id+"F0.wireOp",EDGE,"E14"),sQuery(id+"F0.wireOp",EDGE,"E15"),sQuery(id+"F0.wireOp",EDGE,"E16"),sQuery(id+"F0.wireOp",EDGE,"E17")])],"isStart":true})],"blendedInto":[makeQuery(id+"F1.opExtrude","CAP_FACE",FACE,{"disambiguationData":[OSD([sQuery(id+"F0.wireOp",EDGE,"E0"),sQuery(id+"F0.wireOp",EDGE,"E1"),sQuery(id+"F0.wireOp",EDGE,"E2"),sQuery(id+"F0.wireOp",EDGE,"E3"),subQ1,subQ0,sQuery(id+"F0.wireOp",EDGE,"E6"),sQuery(id+"F0.wireOp",EDGE,"E7"),sQuery(id+"F0.wireOp",EDGE,"E8"),sQuery(id+"F0.wireOp",EDGE,"E9"),sQuery(id+"F0.wireOp",EDGE,"E10"),sQuery(id+"F0.wireOp",EDGE,"E11"),sQuery(id+"F0.wireOp",EDGE,"E12"),sQuery(id+"F0.wireOp",EDGE,"E13"),sQuery(id+"F0.wireOp",EDGE,"E14"),sQuery(id+"F0.wireOp",EDGE,"E15"),sQuery(id+"F0.wireOp",EDGE,"E16"),sQuery(id+"F0.wireOp",EDGE,"E17")])],"isStart":true})]});}
            var Q32;
            {var subQ0=sQuery(id+"F0.wireOp",EDGE,"E12");var subQ1=sQuery(id+"F0.wireOp",EDGE,"E5");Q32=makeQuery(id+"F3.opFillet","BLEND_EDGE",EDGE,{"blendedFrom":[makeQuery(id+"F1.opExtrude","SWEPT_EDGE",EDGE,{"disambiguationData":[OSD([subQ1,subQ0])]}),makeQuery(id+"F1.opExtrude","CAP_FACE",FACE,{"disambiguationData":[OSD([sQuery(id+"F0.wireOp",EDGE,"E0"),sQuery(id+"F0.wireOp",EDGE,"E1"),sQuery(id+"F0.wireOp",EDGE,"E2"),sQuery(id+"F0.wireOp",EDGE,"E3"),sQuery(id+"F0.wireOp",EDGE,"E4"),subQ1,sQuery(id+"F0.wireOp",EDGE,"E6"),sQuery(id+"F0.wireOp",EDGE,"E7"),sQuery(id+"F0.wireOp",EDGE,"E8"),sQuery(id+"F0.wireOp",EDGE,"E9"),sQuery(id+"F0.wireOp",EDGE,"E10"),sQuery(id+"F0.wireOp",EDGE,"E11"),subQ0,sQuery(id+"F0.wireOp",EDGE,"E13"),sQuery(id+"F0.wireOp",EDGE,"E14"),sQuery(id+"F0.wireOp",EDGE,"E15"),sQuery(id+"F0.wireOp",EDGE,"E16"),sQuery(id+"F0.wireOp",EDGE,"E17")])],"isStart":true})],"blendedInto":[makeQuery(id+"F1.opExtrude","CAP_FACE",FACE,{"disambiguationData":[OSD([sQuery(id+"F0.wireOp",EDGE,"E0"),sQuery(id+"F0.wireOp",EDGE,"E1"),sQuery(id+"F0.wireOp",EDGE,"E2"),sQuery(id+"F0.wireOp",EDGE,"E3"),sQuery(id+"F0.wireOp",EDGE,"E4"),subQ1,sQuery(id+"F0.wireOp",EDGE,"E6"),sQuery(id+"F0.wireOp",EDGE,"E7"),sQuery(id+"F0.wireOp",EDGE,"E8"),sQuery(id+"F0.wireOp",EDGE,"E9"),sQuery(id+"F0.wireOp",EDGE,"E10"),sQuery(id+"F0.wireOp",EDGE,"E11"),subQ0,sQuery(id+"F0.wireOp",EDGE,"E13"),sQuery(id+"F0.wireOp",EDGE,"E14"),sQuery(id+"F0.wireOp",EDGE,"E15"),sQuery(id+"F0.wireOp",EDGE,"E16"),sQuery(id+"F0.wireOp",EDGE,"E17")])],"isStart":true})]});}
            var Q33;
            Q33=makeQuery(id+"F1.opExtrude","CAP_EDGE",EDGE,{"disambiguationData":[OSD([sQuery(id+"F0.wireOp",EDGE,"E12")])],"isStart":true});
            var Q34;
            {var subQ0=sQuery(id+"F0.wireOp",EDGE,"E12");var subQ1=sQuery(id+"F0.wireOp",EDGE,"E7");Q34=makeQuery(id+"F3.opFillet","BLEND_EDGE",EDGE,{"blendedFrom":[makeQuery(id+"F2.opChamfer","BLEND_EDGE",EDGE,{"blendedFrom":[makeQuery(id+"F1.opExtrude","SWEPT_EDGE",EDGE,{"disambiguationData":[OSD([subQ1,subQ0])]}),makeQuery(id+"F1.opExtrude","SWEPT_FACE",FACE,{"disambiguationData":[OSD([subQ0])]})],"blendedInto":[makeQuery(id+"F1.opExtrude","SWEPT_FACE",FACE,{"disambiguationData":[OSD([subQ0])]})]}),makeQuery(id+"F1.opExtrude","CAP_FACE",FACE,{"disambiguationData":[OSD([sQuery(id+"F0.wireOp",EDGE,"E0"),sQuery(id+"F0.wireOp",EDGE,"E1"),sQuery(id+"F0.wireOp",EDGE,"E2"),sQuery(id+"F0.wireOp",EDGE,"E3"),sQuery(id+"F0.wireOp",EDGE,"E4"),sQuery(id+"F0.wireOp",EDGE,"E5"),sQuery(id+"F0.wireOp",EDGE,"E6"),subQ1,sQuery(id+"F0.wireOp",EDGE,"E8"),sQuery(id+"F0.wireOp",EDGE,"E9"),sQuery(id+"F0.wireOp",EDGE,"E10"),sQuery(id+"F0.wireOp",EDGE,"E11"),subQ0,sQuery(id+"F0.wireOp",EDGE,"E13"),sQuery(id+"F0.wireOp",EDGE,"E14"),sQuery(id+"F0.wireOp",EDGE,"E15"),sQuery(id+"F0.wireOp",EDGE,"E16"),sQuery(id+"F0.wireOp",EDGE,"E17")])],"isStart":true})],"blendedInto":[makeQuery(id+"F1.opExtrude","CAP_FACE",FACE,{"disambiguationData":[OSD([sQuery(id+"F0.wireOp",EDGE,"E0"),sQuery(id+"F0.wireOp",EDGE,"E1"),sQuery(id+"F0.wireOp",EDGE,"E2"),sQuery(id+"F0.wireOp",EDGE,"E3"),sQuery(id+"F0.wireOp",EDGE,"E4"),sQuery(id+"F0.wireOp",EDGE,"E5"),sQuery(id+"F0.wireOp",EDGE,"E6"),subQ1,sQuery(id+"F0.wireOp",EDGE,"E8"),sQuery(id+"F0.wireOp",EDGE,"E9"),sQuery(id+"F0.wireOp",EDGE,"E10"),sQuery(id+"F0.wireOp",EDGE,"E11"),subQ0,sQuery(id+"F0.wireOp",EDGE,"E13"),sQuery(id+"F0.wireOp",EDGE,"E14"),sQuery(id+"F0.wireOp",EDGE,"E15"),sQuery(id+"F0.wireOp",EDGE,"E16"),sQuery(id+"F0.wireOp",EDGE,"E17")])],"isStart":true})]});}
            var Q35;
            {var subQ0=sQuery(id+"F0.wireOp",EDGE,"E12");var subQ1=sQuery(id+"F0.wireOp",EDGE,"E7");Q35=makeQuery(id+"F2.opChamfer","BLEND_EDGE",EDGE,{"blendedFrom":[makeQuery(id+"F1.opExtrude","SWEPT_EDGE",EDGE,{"disambiguationData":[OSD([subQ1,subQ0])]}),makeQuery(id+"F1.opExtrude","CAP_FACE",FACE,{"disambiguationData":[OSD([sQuery(id+"F0.wireOp",EDGE,"E0"),sQuery(id+"F0.wireOp",EDGE,"E1"),sQuery(id+"F0.wireOp",EDGE,"E2"),sQuery(id+"F0.wireOp",EDGE,"E3"),sQuery(id+"F0.wireOp",EDGE,"E4"),sQuery(id+"F0.wireOp",EDGE,"E5"),sQuery(id+"F0.wireOp",EDGE,"E6"),subQ1,sQuery(id+"F0.wireOp",EDGE,"E8"),sQuery(id+"F0.wireOp",EDGE,"E9"),sQuery(id+"F0.wireOp",EDGE,"E10"),sQuery(id+"F0.wireOp",EDGE,"E11"),subQ0,sQuery(id+"F0.wireOp",EDGE,"E13"),sQuery(id+"F0.wireOp",EDGE,"E14"),sQuery(id+"F0.wireOp",EDGE,"E15"),sQuery(id+"F0.wireOp",EDGE,"E16"),sQuery(id+"F0.wireOp",EDGE,"E17")])],"isStart":true})],"blendedInto":[makeQuery(id+"F1.opExtrude","CAP_FACE",FACE,{"disambiguationData":[OSD([sQuery(id+"F0.wireOp",EDGE,"E0"),sQuery(id+"F0.wireOp",EDGE,"E1"),sQuery(id+"F0.wireOp",EDGE,"E2"),sQuery(id+"F0.wireOp",EDGE,"E3"),sQuery(id+"F0.wireOp",EDGE,"E4"),sQuery(id+"F0.wireOp",EDGE,"E5"),sQuery(id+"F0.wireOp",EDGE,"E6"),subQ1,sQuery(id+"F0.wireOp",EDGE,"E8"),sQuery(id+"F0.wireOp",EDGE,"E9"),sQuery(id+"F0.wireOp",EDGE,"E10"),sQuery(id+"F0.wireOp",EDGE,"E11"),subQ0,sQuery(id+"F0.wireOp",EDGE,"E13"),sQuery(id+"F0.wireOp",EDGE,"E14"),sQuery(id+"F0.wireOp",EDGE,"E15"),sQuery(id+"F0.wireOp",EDGE,"E16"),sQuery(id+"F0.wireOp",EDGE,"E17")])],"isStart":true})]});}
            chamfer(context, id + "F4", {"entities" : qUnion([Q0, Q1, Q2, Q3, Q4, Q5, Q6, Q7, Q8, Q9, Q10, Q11, Q12, Q13, Q14, Q15, Q16, Q17, Q18, Q19, Q20, Q21, Q22, Q23, Q24, Q25, Q26, Q27, Q28, Q29, Q30, Q31, Q32, Q33, Q34, Q35]), "width" : 0.5 * mm, "tangentPropagation" : true});
        }
        {
            var Q0;
            {var subQ0=sQuery(id+"F0.wireOp",EDGE,"E0");Q0=makeQuery(id+"F4.opChamfer","BLEND_EDGE",EDGE,{"blendedFrom":[makeQuery(id+"F1.opExtrude","CAP_EDGE",EDGE,{"disambiguationData":[OSD([subQ0])],"isStart":false}),makeQuery(id+"F1.opExtrude","SWEPT_FACE",FACE,{"disambiguationData":[OSD([subQ0])]})],"blendedInto":[makeQuery(id+"F1.opExtrude","SWEPT_FACE",FACE,{"disambiguationData":[OSD([subQ0])]})]});}
            var Q1;
            {var subQ0=sQuery(id+"F0.wireOp",EDGE,"E1");var subQ1=sQuery(id+"F0.wireOp",EDGE,"E0");Q1=makeQuery(id+"F4.opChamfer","BLEND_EDGE",EDGE,{"blendedFrom":[makeQuery(id+"F3.opFillet","BLEND_EDGE",EDGE,{"blendedFrom":[makeQuery(id+"F1.opExtrude","SWEPT_EDGE",EDGE,{"disambiguationData":[OSD([subQ1,subQ0])]}),makeQuery(id+"F1.opExtrude","CAP_FACE",FACE,{"disambiguationData":[OSD([subQ1,subQ0,sQuery(id+"F0.wireOp",EDGE,"E2"),sQuery(id+"F0.wireOp",EDGE,"E3"),sQuery(id+"F0.wireOp",EDGE,"E4"),sQuery(id+"F0.wireOp",EDGE,"E5"),sQuery(id+"F0.wireOp",EDGE,"E6"),sQuery(id+"F0.wireOp",EDGE,"E7"),sQuery(id+"F0.wireOp",EDGE,"E8"),sQuery(id+"F0.wireOp",EDGE,"E9"),sQuery(id+"F0.wireOp",EDGE,"E10"),sQuery(id+"F0.wireOp",EDGE,"E11"),sQuery(id+"F0.wireOp",EDGE,"E12"),sQuery(id+"F0.wireOp",EDGE,"E13"),sQuery(id+"F0.wireOp",EDGE,"E14"),sQuery(id+"F0.wireOp",EDGE,"E15"),sQuery(id+"F0.wireOp",EDGE,"E16"),sQuery(id+"F0.wireOp",EDGE,"E17")])],"isStart":false})],"blendedInto":[makeQuery(id+"F1.opExtrude","CAP_FACE",FACE,{"disambiguationData":[OSD([subQ1,subQ0,sQuery(id+"F0.wireOp",EDGE,"E2"),sQuery(id+"F0.wireOp",EDGE,"E3"),sQuery(id+"F0.wireOp",EDGE,"E4"),sQuery(id+"F0.wireOp",EDGE,"E5"),sQuery(id+"F0.wireOp",EDGE,"E6"),sQuery(id+"F0.wireOp",EDGE,"E7"),sQuery(id+"F0.wireOp",EDGE,"E8"),sQuery(id+"F0.wireOp",EDGE,"E9"),sQuery(id+"F0.wireOp",EDGE,"E10"),sQuery(id+"F0.wireOp",EDGE,"E11"),sQuery(id+"F0.wireOp",EDGE,"E12"),sQuery(id+"F0.wireOp",EDGE,"E13"),sQuery(id+"F0.wireOp",EDGE,"E14"),sQuery(id+"F0.wireOp",EDGE,"E15"),sQuery(id+"F0.wireOp",EDGE,"E16"),sQuery(id+"F0.wireOp",EDGE,"E17")])],"isStart":false})]}),makeQuery(id+"F3.opFillet","BLEND_FACE",FACE,{"disambiguationData":[OSD([subQ1,subQ0])]})],"blendedInto":[makeQuery(id+"F3.opFillet","BLEND_FACE",FACE,{"disambiguationData":[OSD([subQ1,subQ0])]})]});}
            var Q2;
            {var subQ0=sQuery(id+"F0.wireOp",EDGE,"E1");Q2=makeQuery(id+"F4.opChamfer","BLEND_EDGE",EDGE,{"blendedFrom":[makeQuery(id+"F1.opExtrude","CAP_EDGE",EDGE,{"disambiguationData":[OSD([subQ0])],"isStart":false}),makeQuery(id+"F1.opExtrude","SWEPT_FACE",FACE,{"disambiguationData":[OSD([subQ0])]})],"blendedInto":[makeQuery(id+"F1.opExtrude","SWEPT_FACE",FACE,{"disambiguationData":[OSD([subQ0])]})]});}
            var Q3;
            {var subQ0=sQuery(id+"F0.wireOp",EDGE,"E2");var subQ1=sQuery(id+"F0.wireOp",EDGE,"E1");Q3=makeQuery(id+"F4.opChamfer","BLEND_EDGE",EDGE,{"blendedFrom":[makeQuery(id+"F3.opFillet","BLEND_EDGE",EDGE,{"blendedFrom":[makeQuery(id+"F1.opExtrude","SWEPT_EDGE",EDGE,{"disambiguationData":[OSD([subQ1,subQ0])]}),makeQuery(id+"F1.opExtrude","CAP_FACE",FACE,{"disambiguationData":[OSD([sQuery(id+"F0.wireOp",EDGE,"E0"),subQ1,subQ0,sQuery(id+"F0.wireOp",EDGE,"E3"),sQuery(id+"F0.wireOp",EDGE,"E4"),sQuery(id+"F0.wireOp",EDGE,"E5"),sQuery(id+"F0.wireOp",EDGE,"E6"),sQuery(id+"F0.wireOp",EDGE,"E7"),sQuery(id+"F0.wireOp",EDGE,"E8"),sQuery(id+"F0.wireOp",EDGE,"E9"),sQuery(id+"F0.wireOp",EDGE,"E10"),sQuery(id+"F0.wireOp",EDGE,"E11"),sQuery(id+"F0.wireOp",EDGE,"E12"),sQuery(id+"F0.wireOp",EDGE,"E13"),sQuery(id+"F0.wireOp",EDGE,"E14"),sQuery(id+"F0.wireOp",EDGE,"E15"),sQuery(id+"F0.wireOp",EDGE,"E16"),sQuery(id+"F0.wireOp",EDGE,"E17")])],"isStart":false})],"blendedInto":[makeQuery(id+"F1.opExtrude","CAP_FACE",FACE,{"disambiguationData":[OSD([sQuery(id+"F0.wireOp",EDGE,"E0"),subQ1,subQ0,sQuery(id+"F0.wireOp",EDGE,"E3"),sQuery(id+"F0.wireOp",EDGE,"E4"),sQuery(id+"F0.wireOp",EDGE,"E5"),sQuery(id+"F0.wireOp",EDGE,"E6"),sQuery(id+"F0.wireOp",EDGE,"E7"),sQuery(id+"F0.wireOp",EDGE,"E8"),sQuery(id+"F0.wireOp",EDGE,"E9"),sQuery(id+"F0.wireOp",EDGE,"E10"),sQuery(id+"F0.wireOp",EDGE,"E11"),sQuery(id+"F0.wireOp",EDGE,"E12"),sQuery(id+"F0.wireOp",EDGE,"E13"),sQuery(id+"F0.wireOp",EDGE,"E14"),sQuery(id+"F0.wireOp",EDGE,"E15"),sQuery(id+"F0.wireOp",EDGE,"E16"),sQuery(id+"F0.wireOp",EDGE,"E17")])],"isStart":false})]}),makeQuery(id+"F3.opFillet","BLEND_FACE",FACE,{"disambiguationData":[OSD([subQ1,subQ0])]})],"blendedInto":[makeQuery(id+"F3.opFillet","BLEND_FACE",FACE,{"disambiguationData":[OSD([subQ1,subQ0])]})]});}
            var Q4;
            {var subQ0=sQuery(id+"F0.wireOp",EDGE,"E2");Q4=makeQuery(id+"F4.opChamfer","BLEND_EDGE",EDGE,{"blendedFrom":[makeQuery(id+"F1.opExtrude","CAP_EDGE",EDGE,{"disambiguationData":[OSD([subQ0])],"isStart":false}),makeQuery(id+"F1.opExtrude","SWEPT_FACE",FACE,{"disambiguationData":[OSD([subQ0])]})],"blendedInto":[makeQuery(id+"F1.opExtrude","SWEPT_FACE",FACE,{"disambiguationData":[OSD([subQ0])]})]});}
            var Q5;
            {var subQ0=sQuery(id+"F0.wireOp",EDGE,"E3");var subQ1=sQuery(id+"F0.wireOp",EDGE,"E2");Q5=makeQuery(id+"F4.opChamfer","BLEND_EDGE",EDGE,{"blendedFrom":[makeQuery(id+"F3.opFillet","BLEND_EDGE",EDGE,{"blendedFrom":[makeQuery(id+"F1.opExtrude","SWEPT_EDGE",EDGE,{"disambiguationData":[OSD([subQ1,subQ0])]}),makeQuery(id+"F1.opExtrude","CAP_FACE",FACE,{"disambiguationData":[OSD([sQuery(id+"F0.wireOp",EDGE,"E0"),sQuery(id+"F0.wireOp",EDGE,"E1"),subQ1,subQ0,sQuery(id+"F0.wireOp",EDGE,"E4"),sQuery(id+"F0.wireOp",EDGE,"E5"),sQuery(id+"F0.wireOp",EDGE,"E6"),sQuery(id+"F0.wireOp",EDGE,"E7"),sQuery(id+"F0.wireOp",EDGE,"E8"),sQuery(id+"F0.wireOp",EDGE,"E9"),sQuery(id+"F0.wireOp",EDGE,"E10"),sQuery(id+"F0.wireOp",EDGE,"E11"),sQuery(id+"F0.wireOp",EDGE,"E12"),sQuery(id+"F0.wireOp",EDGE,"E13"),sQuery(id+"F0.wireOp",EDGE,"E14"),sQuery(id+"F0.wireOp",EDGE,"E15"),sQuery(id+"F0.wireOp",EDGE,"E16"),sQuery(id+"F0.wireOp",EDGE,"E17")])],"isStart":false})],"blendedInto":[makeQuery(id+"F1.opExtrude","CAP_FACE",FACE,{"disambiguationData":[OSD([sQuery(id+"F0.wireOp",EDGE,"E0"),sQuery(id+"F0.wireOp",EDGE,"E1"),subQ1,subQ0,sQuery(id+"F0.wireOp",EDGE,"E4"),sQuery(id+"F0.wireOp",EDGE,"E5"),sQuery(id+"F0.wireOp",EDGE,"E6"),sQuery(id+"F0.wireOp",EDGE,"E7"),sQuery(id+"F0.wireOp",EDGE,"E8"),sQuery(id+"F0.wireOp",EDGE,"E9"),sQuery(id+"F0.wireOp",EDGE,"E10"),sQuery(id+"F0.wireOp",EDGE,"E11"),sQuery(id+"F0.wireOp",EDGE,"E12"),sQuery(id+"F0.wireOp",EDGE,"E13"),sQuery(id+"F0.wireOp",EDGE,"E14"),sQuery(id+"F0.wireOp",EDGE,"E15"),sQuery(id+"F0.wireOp",EDGE,"E16"),sQuery(id+"F0.wireOp",EDGE,"E17")])],"isStart":false})]}),makeQuery(id+"F3.opFillet","BLEND_FACE",FACE,{"disambiguationData":[OSD([subQ1,subQ0])]})],"blendedInto":[makeQuery(id+"F3.opFillet","BLEND_FACE",FACE,{"disambiguationData":[OSD([subQ1,subQ0])]})]});}
            var Q6;
            {var subQ0=sQuery(id+"F0.wireOp",EDGE,"E3");Q6=makeQuery(id+"F4.opChamfer","BLEND_EDGE",EDGE,{"blendedFrom":[makeQuery(id+"F1.opExtrude","CAP_EDGE",EDGE,{"disambiguationData":[OSD([subQ0])],"isStart":false}),makeQuery(id+"F1.opExtrude","SWEPT_FACE",FACE,{"disambiguationData":[OSD([subQ0])]})],"blendedInto":[makeQuery(id+"F1.opExtrude","SWEPT_FACE",FACE,{"disambiguationData":[OSD([subQ0])]})]});}
            var Q7;
            {var subQ0=sQuery(id+"F0.wireOp",EDGE,"E4");var subQ1=sQuery(id+"F0.wireOp",EDGE,"E3");Q7=makeQuery(id+"F4.opChamfer","BLEND_EDGE",EDGE,{"blendedFrom":[makeQuery(id+"F3.opFillet","BLEND_EDGE",EDGE,{"blendedFrom":[makeQuery(id+"F1.opExtrude","SWEPT_EDGE",EDGE,{"disambiguationData":[OSD([subQ1,subQ0])]}),makeQuery(id+"F1.opExtrude","CAP_FACE",FACE,{"disambiguationData":[OSD([sQuery(id+"F0.wireOp",EDGE,"E0"),sQuery(id+"F0.wireOp",EDGE,"E1"),sQuery(id+"F0.wireOp",EDGE,"E2"),subQ1,subQ0,sQuery(id+"F0.wireOp",EDGE,"E5"),sQuery(id+"F0.wireOp",EDGE,"E6"),sQuery(id+"F0.wireOp",EDGE,"E7"),sQuery(id+"F0.wireOp",EDGE,"E8"),sQuery(id+"F0.wireOp",EDGE,"E9"),sQuery(id+"F0.wireOp",EDGE,"E10"),sQuery(id+"F0.wireOp",EDGE,"E11"),sQuery(id+"F0.wireOp",EDGE,"E12"),sQuery(id+"F0.wireOp",EDGE,"E13"),sQuery(id+"F0.wireOp",EDGE,"E14"),sQuery(id+"F0.wireOp",EDGE,"E15"),sQuery(id+"F0.wireOp",EDGE,"E16"),sQuery(id+"F0.wireOp",EDGE,"E17")])],"isStart":false})],"blendedInto":[makeQuery(id+"F1.opExtrude","CAP_FACE",FACE,{"disambiguationData":[OSD([sQuery(id+"F0.wireOp",EDGE,"E0"),sQuery(id+"F0.wireOp",EDGE,"E1"),sQuery(id+"F0.wireOp",EDGE,"E2"),subQ1,subQ0,sQuery(id+"F0.wireOp",EDGE,"E5"),sQuery(id+"F0.wireOp",EDGE,"E6"),sQuery(id+"F0.wireOp",EDGE,"E7"),sQuery(id+"F0.wireOp",EDGE,"E8"),sQuery(id+"F0.wireOp",EDGE,"E9"),sQuery(id+"F0.wireOp",EDGE,"E10"),sQuery(id+"F0.wireOp",EDGE,"E11"),sQuery(id+"F0.wireOp",EDGE,"E12"),sQuery(id+"F0.wireOp",EDGE,"E13"),sQuery(id+"F0.wireOp",EDGE,"E14"),sQuery(id+"F0.wireOp",EDGE,"E15"),sQuery(id+"F0.wireOp",EDGE,"E16"),sQuery(id+"F0.wireOp",EDGE,"E17")])],"isStart":false})]}),makeQuery(id+"F3.opFillet","BLEND_FACE",FACE,{"disambiguationData":[OSD([subQ1,subQ0])]})],"blendedInto":[makeQuery(id+"F3.opFillet","BLEND_FACE",FACE,{"disambiguationData":[OSD([subQ1,subQ0])]})]});}
            var Q8;
            {var subQ0=sQuery(id+"F0.wireOp",EDGE,"E4");Q8=makeQuery(id+"F4.opChamfer","BLEND_EDGE",EDGE,{"blendedFrom":[makeQuery(id+"F1.opExtrude","CAP_EDGE",EDGE,{"disambiguationData":[OSD([subQ0])],"isStart":false}),makeQuery(id+"F1.opExtrude","SWEPT_FACE",FACE,{"disambiguationData":[OSD([subQ0])]})],"blendedInto":[makeQuery(id+"F1.opExtrude","SWEPT_FACE",FACE,{"disambiguationData":[OSD([subQ0])]})]});}
            var Q9;
            {var subQ0=sQuery(id+"F0.wireOp",EDGE,"E5");var subQ1=sQuery(id+"F0.wireOp",EDGE,"E4");Q9=makeQuery(id+"F4.opChamfer","BLEND_EDGE",EDGE,{"blendedFrom":[makeQuery(id+"F3.opFillet","BLEND_EDGE",EDGE,{"blendedFrom":[makeQuery(id+"F1.opExtrude","SWEPT_EDGE",EDGE,{"disambiguationData":[OSD([subQ1,subQ0])]}),makeQuery(id+"F1.opExtrude","CAP_FACE",FACE,{"disambiguationData":[OSD([sQuery(id+"F0.wireOp",EDGE,"E0"),sQuery(id+"F0.wireOp",EDGE,"E1"),sQuery(id+"F0.wireOp",EDGE,"E2"),sQuery(id+"F0.wireOp",EDGE,"E3"),subQ1,subQ0,sQuery(id+"F0.wireOp",EDGE,"E6"),sQuery(id+"F0.wireOp",EDGE,"E7"),sQuery(id+"F0.wireOp",EDGE,"E8"),sQuery(id+"F0.wireOp",EDGE,"E9"),sQuery(id+"F0.wireOp",EDGE,"E10"),sQuery(id+"F0.wireOp",EDGE,"E11"),sQuery(id+"F0.wireOp",EDGE,"E12"),sQuery(id+"F0.wireOp",EDGE,"E13"),sQuery(id+"F0.wireOp",EDGE,"E14"),sQuery(id+"F0.wireOp",EDGE,"E15"),sQuery(id+"F0.wireOp",EDGE,"E16"),sQuery(id+"F0.wireOp",EDGE,"E17")])],"isStart":false})],"blendedInto":[makeQuery(id+"F1.opExtrude","CAP_FACE",FACE,{"disambiguationData":[OSD([sQuery(id+"F0.wireOp",EDGE,"E0"),sQuery(id+"F0.wireOp",EDGE,"E1"),sQuery(id+"F0.wireOp",EDGE,"E2"),sQuery(id+"F0.wireOp",EDGE,"E3"),subQ1,subQ0,sQuery(id+"F0.wireOp",EDGE,"E6"),sQuery(id+"F0.wireOp",EDGE,"E7"),sQuery(id+"F0.wireOp",EDGE,"E8"),sQuery(id+"F0.wireOp",EDGE,"E9"),sQuery(id+"F0.wireOp",EDGE,"E10"),sQuery(id+"F0.wireOp",EDGE,"E11"),sQuery(id+"F0.wireOp",EDGE,"E12"),sQuery(id+"F0.wireOp",EDGE,"E13"),sQuery(id+"F0.wireOp",EDGE,"E14"),sQuery(id+"F0.wireOp",EDGE,"E15"),sQuery(id+"F0.wireOp",EDGE,"E16"),sQuery(id+"F0.wireOp",EDGE,"E17")])],"isStart":false})]}),makeQuery(id+"F3.opFillet","BLEND_FACE",FACE,{"disambiguationData":[OSD([subQ1,subQ0])]})],"blendedInto":[makeQuery(id+"F3.opFillet","BLEND_FACE",FACE,{"disambiguationData":[OSD([subQ1,subQ0])]})]});}
            var Q10;
            {var subQ0=sQuery(id+"F0.wireOp",EDGE,"E5");Q10=makeQuery(id+"F4.opChamfer","BLEND_EDGE",EDGE,{"blendedFrom":[makeQuery(id+"F1.opExtrude","CAP_EDGE",EDGE,{"disambiguationData":[OSD([subQ0])],"isStart":false}),makeQuery(id+"F1.opExtrude","SWEPT_FACE",FACE,{"disambiguationData":[OSD([subQ0])]})],"blendedInto":[makeQuery(id+"F1.opExtrude","SWEPT_FACE",FACE,{"disambiguationData":[OSD([subQ0])]})]});}
            var Q11;
            {var subQ0=sQuery(id+"F0.wireOp",EDGE,"E12");Q11=makeQuery(id+"F4.opChamfer","BLEND_EDGE",EDGE,{"blendedFrom":[makeQuery(id+"F1.opExtrude","CAP_EDGE",EDGE,{"disambiguationData":[OSD([subQ0])],"isStart":false}),makeQuery(id+"F1.opExtrude","SWEPT_FACE",FACE,{"disambiguationData":[OSD([subQ0])]})],"blendedInto":[makeQuery(id+"F1.opExtrude","SWEPT_FACE",FACE,{"disambiguationData":[OSD([subQ0])]})]});}
            var Q12;
            {var subQ0=sQuery(id+"F0.wireOp",EDGE,"E12");var subQ1=sQuery(id+"F0.wireOp",EDGE,"E5");Q12=makeQuery(id+"F4.opChamfer","BLEND_EDGE",EDGE,{"blendedFrom":[makeQuery(id+"F3.opFillet","BLEND_EDGE",EDGE,{"blendedFrom":[makeQuery(id+"F1.opExtrude","SWEPT_EDGE",EDGE,{"disambiguationData":[OSD([subQ1,subQ0])]}),makeQuery(id+"F1.opExtrude","CAP_FACE",FACE,{"disambiguationData":[OSD([sQuery(id+"F0.wireOp",EDGE,"E0"),sQuery(id+"F0.wireOp",EDGE,"E1"),sQuery(id+"F0.wireOp",EDGE,"E2"),sQuery(id+"F0.wireOp",EDGE,"E3"),sQuery(id+"F0.wireOp",EDGE,"E4"),subQ1,sQuery(id+"F0.wireOp",EDGE,"E6"),sQuery(id+"F0.wireOp",EDGE,"E7"),sQuery(id+"F0.wireOp",EDGE,"E8"),sQuery(id+"F0.wireOp",EDGE,"E9"),sQuery(id+"F0.wireOp",EDGE,"E10"),sQuery(id+"F0.wireOp",EDGE,"E11"),subQ0,sQuery(id+"F0.wireOp",EDGE,"E13"),sQuery(id+"F0.wireOp",EDGE,"E14"),sQuery(id+"F0.wireOp",EDGE,"E15"),sQuery(id+"F0.wireOp",EDGE,"E16"),sQuery(id+"F0.wireOp",EDGE,"E17")])],"isStart":false})],"blendedInto":[makeQuery(id+"F1.opExtrude","CAP_FACE",FACE,{"disambiguationData":[OSD([sQuery(id+"F0.wireOp",EDGE,"E0"),sQuery(id+"F0.wireOp",EDGE,"E1"),sQuery(id+"F0.wireOp",EDGE,"E2"),sQuery(id+"F0.wireOp",EDGE,"E3"),sQuery(id+"F0.wireOp",EDGE,"E4"),subQ1,sQuery(id+"F0.wireOp",EDGE,"E6"),sQuery(id+"F0.wireOp",EDGE,"E7"),sQuery(id+"F0.wireOp",EDGE,"E8"),sQuery(id+"F0.wireOp",EDGE,"E9"),sQuery(id+"F0.wireOp",EDGE,"E10"),sQuery(id+"F0.wireOp",EDGE,"E11"),subQ0,sQuery(id+"F0.wireOp",EDGE,"E13"),sQuery(id+"F0.wireOp",EDGE,"E14"),sQuery(id+"F0.wireOp",EDGE,"E15"),sQuery(id+"F0.wireOp",EDGE,"E16"),sQuery(id+"F0.wireOp",EDGE,"E17")])],"isStart":false})]}),makeQuery(id+"F3.opFillet","BLEND_FACE",FACE,{"disambiguationData":[OSD([subQ1,subQ0])]})],"blendedInto":[makeQuery(id+"F3.opFillet","BLEND_FACE",FACE,{"disambiguationData":[OSD([subQ1,subQ0])]})]});}
            var Q13;
            {var subQ0=sQuery(id+"F0.wireOp",EDGE,"E12");var subQ1=sQuery(id+"F0.wireOp",EDGE,"E7");Q13=makeQuery(id+"F4.opChamfer","BLEND_EDGE",EDGE,{"blendedFrom":[makeQuery(id+"F3.opFillet","BLEND_EDGE",EDGE,{"blendedFrom":[makeQuery(id+"F2.opChamfer","BLEND_EDGE",EDGE,{"blendedFrom":[makeQuery(id+"F1.opExtrude","SWEPT_EDGE",EDGE,{"disambiguationData":[OSD([subQ1,subQ0])]}),makeQuery(id+"F1.opExtrude","SWEPT_FACE",FACE,{"disambiguationData":[OSD([subQ0])]})],"blendedInto":[makeQuery(id+"F1.opExtrude","SWEPT_FACE",FACE,{"disambiguationData":[OSD([subQ0])]})]}),makeQuery(id+"F1.opExtrude","CAP_FACE",FACE,{"disambiguationData":[OSD([sQuery(id+"F0.wireOp",EDGE,"E0"),sQuery(id+"F0.wireOp",EDGE,"E1"),sQuery(id+"F0.wireOp",EDGE,"E2"),sQuery(id+"F0.wireOp",EDGE,"E3"),sQuery(id+"F0.wireOp",EDGE,"E4"),sQuery(id+"F0.wireOp",EDGE,"E5"),sQuery(id+"F0.wireOp",EDGE,"E6"),subQ1,sQuery(id+"F0.wireOp",EDGE,"E8"),sQuery(id+"F0.wireOp",EDGE,"E9"),sQuery(id+"F0.wireOp",EDGE,"E10"),sQuery(id+"F0.wireOp",EDGE,"E11"),subQ0,sQuery(id+"F0.wireOp",EDGE,"E13"),sQuery(id+"F0.wireOp",EDGE,"E14"),sQuery(id+"F0.wireOp",EDGE,"E15"),sQuery(id+"F0.wireOp",EDGE,"E16"),sQuery(id+"F0.wireOp",EDGE,"E17")])],"isStart":false})],"blendedInto":[makeQuery(id+"F1.opExtrude","CAP_FACE",FACE,{"disambiguationData":[OSD([sQuery(id+"F0.wireOp",EDGE,"E0"),sQuery(id+"F0.wireOp",EDGE,"E1"),sQuery(id+"F0.wireOp",EDGE,"E2"),sQuery(id+"F0.wireOp",EDGE,"E3"),sQuery(id+"F0.wireOp",EDGE,"E4"),sQuery(id+"F0.wireOp",EDGE,"E5"),sQuery(id+"F0.wireOp",EDGE,"E6"),subQ1,sQuery(id+"F0.wireOp",EDGE,"E8"),sQuery(id+"F0.wireOp",EDGE,"E9"),sQuery(id+"F0.wireOp",EDGE,"E10"),sQuery(id+"F0.wireOp",EDGE,"E11"),subQ0,sQuery(id+"F0.wireOp",EDGE,"E13"),sQuery(id+"F0.wireOp",EDGE,"E14"),sQuery(id+"F0.wireOp",EDGE,"E15"),sQuery(id+"F0.wireOp",EDGE,"E16"),sQuery(id+"F0.wireOp",EDGE,"E17")])],"isStart":false})]}),makeQuery(id+"F3.opFillet","BLEND_FACE",FACE,{"disambiguationData":[OSD([subQ1,subQ0])]})],"blendedInto":[makeQuery(id+"F3.opFillet","BLEND_FACE",FACE,{"disambiguationData":[OSD([subQ1,subQ0])]})]});}
            var Q14;
            {var subQ0=sQuery(id+"F0.wireOp",EDGE,"E12");var subQ1=sQuery(id+"F0.wireOp",EDGE,"E7");Q14=makeQuery(id+"F4.opChamfer","BLEND_EDGE",EDGE,{"blendedFrom":[makeQuery(id+"F2.opChamfer","BLEND_EDGE",EDGE,{"blendedFrom":[makeQuery(id+"F1.opExtrude","SWEPT_EDGE",EDGE,{"disambiguationData":[OSD([subQ1,subQ0])]}),makeQuery(id+"F1.opExtrude","CAP_FACE",FACE,{"disambiguationData":[OSD([sQuery(id+"F0.wireOp",EDGE,"E0"),sQuery(id+"F0.wireOp",EDGE,"E1"),sQuery(id+"F0.wireOp",EDGE,"E2"),sQuery(id+"F0.wireOp",EDGE,"E3"),sQuery(id+"F0.wireOp",EDGE,"E4"),sQuery(id+"F0.wireOp",EDGE,"E5"),sQuery(id+"F0.wireOp",EDGE,"E6"),subQ1,sQuery(id+"F0.wireOp",EDGE,"E8"),sQuery(id+"F0.wireOp",EDGE,"E9"),sQuery(id+"F0.wireOp",EDGE,"E10"),sQuery(id+"F0.wireOp",EDGE,"E11"),subQ0,sQuery(id+"F0.wireOp",EDGE,"E13"),sQuery(id+"F0.wireOp",EDGE,"E14"),sQuery(id+"F0.wireOp",EDGE,"E15"),sQuery(id+"F0.wireOp",EDGE,"E16"),sQuery(id+"F0.wireOp",EDGE,"E17")])],"isStart":false})],"blendedInto":[makeQuery(id+"F1.opExtrude","CAP_FACE",FACE,{"disambiguationData":[OSD([sQuery(id+"F0.wireOp",EDGE,"E0"),sQuery(id+"F0.wireOp",EDGE,"E1"),sQuery(id+"F0.wireOp",EDGE,"E2"),sQuery(id+"F0.wireOp",EDGE,"E3"),sQuery(id+"F0.wireOp",EDGE,"E4"),sQuery(id+"F0.wireOp",EDGE,"E5"),sQuery(id+"F0.wireOp",EDGE,"E6"),subQ1,sQuery(id+"F0.wireOp",EDGE,"E8"),sQuery(id+"F0.wireOp",EDGE,"E9"),sQuery(id+"F0.wireOp",EDGE,"E10"),sQuery(id+"F0.wireOp",EDGE,"E11"),subQ0,sQuery(id+"F0.wireOp",EDGE,"E13"),sQuery(id+"F0.wireOp",EDGE,"E14"),sQuery(id+"F0.wireOp",EDGE,"E15"),sQuery(id+"F0.wireOp",EDGE,"E16"),sQuery(id+"F0.wireOp",EDGE,"E17")])],"isStart":false})]}),makeQuery(id+"F2.opChamfer","BLEND_FACE",FACE,{"disambiguationData":[OSD([subQ1,subQ0])]})],"blendedInto":[makeQuery(id+"F2.opChamfer","BLEND_FACE",FACE,{"disambiguationData":[OSD([subQ1,subQ0])]})]});}
            var Q15;
            {var subQ0=sQuery(id+"F0.wireOp",EDGE,"E11");var subQ1=sQuery(id+"F0.wireOp",EDGE,"E6");Q15=makeQuery(id+"F4.opChamfer","BLEND_EDGE",EDGE,{"blendedFrom":[makeQuery(id+"F1.opExtrude","CAP_EDGE",EDGE,{"disambiguationData":[OSD([subQ1,subQ0])],"isStart":false}),makeQuery(id+"F1.opExtrude","SWEPT_FACE",FACE,{"disambiguationData":[OSD([subQ1,subQ0])]})],"blendedInto":[makeQuery(id+"F1.opExtrude","SWEPT_FACE",FACE,{"disambiguationData":[OSD([subQ1,subQ0])]})]});}
            var Q16;
            {var subQ0=sQuery(id+"F0.wireOp",EDGE,"E11");var subQ1=sQuery(id+"F0.wireOp",EDGE,"E6");Q16=makeQuery(id+"F4.opChamfer","BLEND_EDGE",EDGE,{"blendedFrom":[makeQuery(id+"F1.opExtrude","CAP_EDGE",EDGE,{"disambiguationData":[OSD([subQ1,subQ0])],"isStart":true}),makeQuery(id+"F1.opExtrude","SWEPT_FACE",FACE,{"disambiguationData":[OSD([subQ1,subQ0])]})],"blendedInto":[makeQuery(id+"F1.opExtrude","SWEPT_FACE",FACE,{"disambiguationData":[OSD([subQ1,subQ0])]})]});}
            var Q17;
            {var subQ0=sQuery(id+"F0.wireOp",EDGE,"E0");Q17=makeQuery(id+"F4.opChamfer","BLEND_EDGE",EDGE,{"blendedFrom":[makeQuery(id+"F1.opExtrude","CAP_EDGE",EDGE,{"disambiguationData":[OSD([subQ0])],"isStart":true}),makeQuery(id+"F1.opExtrude","SWEPT_FACE",FACE,{"disambiguationData":[OSD([subQ0])]})],"blendedInto":[makeQuery(id+"F1.opExtrude","SWEPT_FACE",FACE,{"disambiguationData":[OSD([subQ0])]})]});}
            var Q18;
            {var subQ0=sQuery(id+"F0.wireOp",EDGE,"E1");var subQ1=sQuery(id+"F0.wireOp",EDGE,"E0");Q18=makeQuery(id+"F4.opChamfer","BLEND_EDGE",EDGE,{"blendedFrom":[makeQuery(id+"F3.opFillet","BLEND_EDGE",EDGE,{"blendedFrom":[makeQuery(id+"F1.opExtrude","SWEPT_EDGE",EDGE,{"disambiguationData":[OSD([subQ1,subQ0])]}),makeQuery(id+"F1.opExtrude","CAP_FACE",FACE,{"disambiguationData":[OSD([subQ1,subQ0,sQuery(id+"F0.wireOp",EDGE,"E2"),sQuery(id+"F0.wireOp",EDGE,"E3"),sQuery(id+"F0.wireOp",EDGE,"E4"),sQuery(id+"F0.wireOp",EDGE,"E5"),sQuery(id+"F0.wireOp",EDGE,"E6"),sQuery(id+"F0.wireOp",EDGE,"E7"),sQuery(id+"F0.wireOp",EDGE,"E8"),sQuery(id+"F0.wireOp",EDGE,"E9"),sQuery(id+"F0.wireOp",EDGE,"E10"),sQuery(id+"F0.wireOp",EDGE,"E11"),sQuery(id+"F0.wireOp",EDGE,"E12"),sQuery(id+"F0.wireOp",EDGE,"E13"),sQuery(id+"F0.wireOp",EDGE,"E14"),sQuery(id+"F0.wireOp",EDGE,"E15"),sQuery(id+"F0.wireOp",EDGE,"E16"),sQuery(id+"F0.wireOp",EDGE,"E17")])],"isStart":true})],"blendedInto":[makeQuery(id+"F1.opExtrude","CAP_FACE",FACE,{"disambiguationData":[OSD([subQ1,subQ0,sQuery(id+"F0.wireOp",EDGE,"E2"),sQuery(id+"F0.wireOp",EDGE,"E3"),sQuery(id+"F0.wireOp",EDGE,"E4"),sQuery(id+"F0.wireOp",EDGE,"E5"),sQuery(id+"F0.wireOp",EDGE,"E6"),sQuery(id+"F0.wireOp",EDGE,"E7"),sQuery(id+"F0.wireOp",EDGE,"E8"),sQuery(id+"F0.wireOp",EDGE,"E9"),sQuery(id+"F0.wireOp",EDGE,"E10"),sQuery(id+"F0.wireOp",EDGE,"E11"),sQuery(id+"F0.wireOp",EDGE,"E12"),sQuery(id+"F0.wireOp",EDGE,"E13"),sQuery(id+"F0.wireOp",EDGE,"E14"),sQuery(id+"F0.wireOp",EDGE,"E15"),sQuery(id+"F0.wireOp",EDGE,"E16"),sQuery(id+"F0.wireOp",EDGE,"E17")])],"isStart":true})]}),makeQuery(id+"F3.opFillet","BLEND_FACE",FACE,{"disambiguationData":[OSD([subQ1,subQ0])]})],"blendedInto":[makeQuery(id+"F3.opFillet","BLEND_FACE",FACE,{"disambiguationData":[OSD([subQ1,subQ0])]})]});}
            var Q19;
            {var subQ0=sQuery(id+"F0.wireOp",EDGE,"E1");Q19=makeQuery(id+"F4.opChamfer","BLEND_EDGE",EDGE,{"blendedFrom":[makeQuery(id+"F1.opExtrude","CAP_EDGE",EDGE,{"disambiguationData":[OSD([subQ0])],"isStart":true}),makeQuery(id+"F1.opExtrude","SWEPT_FACE",FACE,{"disambiguationData":[OSD([subQ0])]})],"blendedInto":[makeQuery(id+"F1.opExtrude","SWEPT_FACE",FACE,{"disambiguationData":[OSD([subQ0])]})]});}
            var Q20;
            {var subQ0=sQuery(id+"F0.wireOp",EDGE,"E2");var subQ1=sQuery(id+"F0.wireOp",EDGE,"E1");Q20=makeQuery(id+"F4.opChamfer","BLEND_EDGE",EDGE,{"blendedFrom":[makeQuery(id+"F3.opFillet","BLEND_EDGE",EDGE,{"blendedFrom":[makeQuery(id+"F1.opExtrude","SWEPT_EDGE",EDGE,{"disambiguationData":[OSD([subQ1,subQ0])]}),makeQuery(id+"F1.opExtrude","CAP_FACE",FACE,{"disambiguationData":[OSD([sQuery(id+"F0.wireOp",EDGE,"E0"),subQ1,subQ0,sQuery(id+"F0.wireOp",EDGE,"E3"),sQuery(id+"F0.wireOp",EDGE,"E4"),sQuery(id+"F0.wireOp",EDGE,"E5"),sQuery(id+"F0.wireOp",EDGE,"E6"),sQuery(id+"F0.wireOp",EDGE,"E7"),sQuery(id+"F0.wireOp",EDGE,"E8"),sQuery(id+"F0.wireOp",EDGE,"E9"),sQuery(id+"F0.wireOp",EDGE,"E10"),sQuery(id+"F0.wireOp",EDGE,"E11"),sQuery(id+"F0.wireOp",EDGE,"E12"),sQuery(id+"F0.wireOp",EDGE,"E13"),sQuery(id+"F0.wireOp",EDGE,"E14"),sQuery(id+"F0.wireOp",EDGE,"E15"),sQuery(id+"F0.wireOp",EDGE,"E16"),sQuery(id+"F0.wireOp",EDGE,"E17")])],"isStart":true})],"blendedInto":[makeQuery(id+"F1.opExtrude","CAP_FACE",FACE,{"disambiguationData":[OSD([sQuery(id+"F0.wireOp",EDGE,"E0"),subQ1,subQ0,sQuery(id+"F0.wireOp",EDGE,"E3"),sQuery(id+"F0.wireOp",EDGE,"E4"),sQuery(id+"F0.wireOp",EDGE,"E5"),sQuery(id+"F0.wireOp",EDGE,"E6"),sQuery(id+"F0.wireOp",EDGE,"E7"),sQuery(id+"F0.wireOp",EDGE,"E8"),sQuery(id+"F0.wireOp",EDGE,"E9"),sQuery(id+"F0.wireOp",EDGE,"E10"),sQuery(id+"F0.wireOp",EDGE,"E11"),sQuery(id+"F0.wireOp",EDGE,"E12"),sQuery(id+"F0.wireOp",EDGE,"E13"),sQuery(id+"F0.wireOp",EDGE,"E14"),sQuery(id+"F0.wireOp",EDGE,"E15"),sQuery(id+"F0.wireOp",EDGE,"E16"),sQuery(id+"F0.wireOp",EDGE,"E17")])],"isStart":true})]}),makeQuery(id+"F3.opFillet","BLEND_FACE",FACE,{"disambiguationData":[OSD([subQ1,subQ0])]})],"blendedInto":[makeQuery(id+"F3.opFillet","BLEND_FACE",FACE,{"disambiguationData":[OSD([subQ1,subQ0])]})]});}
            var Q21;
            {var subQ0=sQuery(id+"F0.wireOp",EDGE,"E2");Q21=makeQuery(id+"F4.opChamfer","BLEND_EDGE",EDGE,{"blendedFrom":[makeQuery(id+"F1.opExtrude","CAP_EDGE",EDGE,{"disambiguationData":[OSD([subQ0])],"isStart":true}),makeQuery(id+"F1.opExtrude","SWEPT_FACE",FACE,{"disambiguationData":[OSD([subQ0])]})],"blendedInto":[makeQuery(id+"F1.opExtrude","SWEPT_FACE",FACE,{"disambiguationData":[OSD([subQ0])]})]});}
            var Q22;
            {var subQ0=sQuery(id+"F0.wireOp",EDGE,"E3");var subQ1=sQuery(id+"F0.wireOp",EDGE,"E2");Q22=makeQuery(id+"F4.opChamfer","BLEND_EDGE",EDGE,{"blendedFrom":[makeQuery(id+"F3.opFillet","BLEND_EDGE",EDGE,{"blendedFrom":[makeQuery(id+"F1.opExtrude","SWEPT_EDGE",EDGE,{"disambiguationData":[OSD([subQ1,subQ0])]}),makeQuery(id+"F1.opExtrude","CAP_FACE",FACE,{"disambiguationData":[OSD([sQuery(id+"F0.wireOp",EDGE,"E0"),sQuery(id+"F0.wireOp",EDGE,"E1"),subQ1,subQ0,sQuery(id+"F0.wireOp",EDGE,"E4"),sQuery(id+"F0.wireOp",EDGE,"E5"),sQuery(id+"F0.wireOp",EDGE,"E6"),sQuery(id+"F0.wireOp",EDGE,"E7"),sQuery(id+"F0.wireOp",EDGE,"E8"),sQuery(id+"F0.wireOp",EDGE,"E9"),sQuery(id+"F0.wireOp",EDGE,"E10"),sQuery(id+"F0.wireOp",EDGE,"E11"),sQuery(id+"F0.wireOp",EDGE,"E12"),sQuery(id+"F0.wireOp",EDGE,"E13"),sQuery(id+"F0.wireOp",EDGE,"E14"),sQuery(id+"F0.wireOp",EDGE,"E15"),sQuery(id+"F0.wireOp",EDGE,"E16"),sQuery(id+"F0.wireOp",EDGE,"E17")])],"isStart":true})],"blendedInto":[makeQuery(id+"F1.opExtrude","CAP_FACE",FACE,{"disambiguationData":[OSD([sQuery(id+"F0.wireOp",EDGE,"E0"),sQuery(id+"F0.wireOp",EDGE,"E1"),subQ1,subQ0,sQuery(id+"F0.wireOp",EDGE,"E4"),sQuery(id+"F0.wireOp",EDGE,"E5"),sQuery(id+"F0.wireOp",EDGE,"E6"),sQuery(id+"F0.wireOp",EDGE,"E7"),sQuery(id+"F0.wireOp",EDGE,"E8"),sQuery(id+"F0.wireOp",EDGE,"E9"),sQuery(id+"F0.wireOp",EDGE,"E10"),sQuery(id+"F0.wireOp",EDGE,"E11"),sQuery(id+"F0.wireOp",EDGE,"E12"),sQuery(id+"F0.wireOp",EDGE,"E13"),sQuery(id+"F0.wireOp",EDGE,"E14"),sQuery(id+"F0.wireOp",EDGE,"E15"),sQuery(id+"F0.wireOp",EDGE,"E16"),sQuery(id+"F0.wireOp",EDGE,"E17")])],"isStart":true})]}),makeQuery(id+"F3.opFillet","BLEND_FACE",FACE,{"disambiguationData":[OSD([subQ1,subQ0])]})],"blendedInto":[makeQuery(id+"F3.opFillet","BLEND_FACE",FACE,{"disambiguationData":[OSD([subQ1,subQ0])]})]});}
            var Q23;
            {var subQ0=sQuery(id+"F0.wireOp",EDGE,"E3");Q23=makeQuery(id+"F4.opChamfer","BLEND_EDGE",EDGE,{"blendedFrom":[makeQuery(id+"F1.opExtrude","CAP_EDGE",EDGE,{"disambiguationData":[OSD([subQ0])],"isStart":true}),makeQuery(id+"F1.opExtrude","SWEPT_FACE",FACE,{"disambiguationData":[OSD([subQ0])]})],"blendedInto":[makeQuery(id+"F1.opExtrude","SWEPT_FACE",FACE,{"disambiguationData":[OSD([subQ0])]})]});}
            var Q24;
            {var subQ0=sQuery(id+"F0.wireOp",EDGE,"E4");Q24=makeQuery(id+"F4.opChamfer","BLEND_EDGE",EDGE,{"blendedFrom":[makeQuery(id+"F1.opExtrude","CAP_EDGE",EDGE,{"disambiguationData":[OSD([subQ0])],"isStart":true}),makeQuery(id+"F1.opExtrude","SWEPT_FACE",FACE,{"disambiguationData":[OSD([subQ0])]})],"blendedInto":[makeQuery(id+"F1.opExtrude","SWEPT_FACE",FACE,{"disambiguationData":[OSD([subQ0])]})]});}
            var Q25;
            {var subQ0=sQuery(id+"F0.wireOp",EDGE,"E4");var subQ1=sQuery(id+"F0.wireOp",EDGE,"E3");Q25=makeQuery(id+"F4.opChamfer","BLEND_EDGE",EDGE,{"blendedFrom":[makeQuery(id+"F3.opFillet","BLEND_EDGE",EDGE,{"blendedFrom":[makeQuery(id+"F1.opExtrude","SWEPT_EDGE",EDGE,{"disambiguationData":[OSD([subQ1,subQ0])]}),makeQuery(id+"F1.opExtrude","CAP_FACE",FACE,{"disambiguationData":[OSD([sQuery(id+"F0.wireOp",EDGE,"E0"),sQuery(id+"F0.wireOp",EDGE,"E1"),sQuery(id+"F0.wireOp",EDGE,"E2"),subQ1,subQ0,sQuery(id+"F0.wireOp",EDGE,"E5"),sQuery(id+"F0.wireOp",EDGE,"E6"),sQuery(id+"F0.wireOp",EDGE,"E7"),sQuery(id+"F0.wireOp",EDGE,"E8"),sQuery(id+"F0.wireOp",EDGE,"E9"),sQuery(id+"F0.wireOp",EDGE,"E10"),sQuery(id+"F0.wireOp",EDGE,"E11"),sQuery(id+"F0.wireOp",EDGE,"E12"),sQuery(id+"F0.wireOp",EDGE,"E13"),sQuery(id+"F0.wireOp",EDGE,"E14"),sQuery(id+"F0.wireOp",EDGE,"E15"),sQuery(id+"F0.wireOp",EDGE,"E16"),sQuery(id+"F0.wireOp",EDGE,"E17")])],"isStart":true})],"blendedInto":[makeQuery(id+"F1.opExtrude","CAP_FACE",FACE,{"disambiguationData":[OSD([sQuery(id+"F0.wireOp",EDGE,"E0"),sQuery(id+"F0.wireOp",EDGE,"E1"),sQuery(id+"F0.wireOp",EDGE,"E2"),subQ1,subQ0,sQuery(id+"F0.wireOp",EDGE,"E5"),sQuery(id+"F0.wireOp",EDGE,"E6"),sQuery(id+"F0.wireOp",EDGE,"E7"),sQuery(id+"F0.wireOp",EDGE,"E8"),sQuery(id+"F0.wireOp",EDGE,"E9"),sQuery(id+"F0.wireOp",EDGE,"E10"),sQuery(id+"F0.wireOp",EDGE,"E11"),sQuery(id+"F0.wireOp",EDGE,"E12"),sQuery(id+"F0.wireOp",EDGE,"E13"),sQuery(id+"F0.wireOp",EDGE,"E14"),sQuery(id+"F0.wireOp",EDGE,"E15"),sQuery(id+"F0.wireOp",EDGE,"E16"),sQuery(id+"F0.wireOp",EDGE,"E17")])],"isStart":true})]}),makeQuery(id+"F3.opFillet","BLEND_FACE",FACE,{"disambiguationData":[OSD([subQ1,subQ0])]})],"blendedInto":[makeQuery(id+"F3.opFillet","BLEND_FACE",FACE,{"disambiguationData":[OSD([subQ1,subQ0])]})]});}
            var Q26;
            {var subQ0=sQuery(id+"F0.wireOp",EDGE,"E5");var subQ1=sQuery(id+"F0.wireOp",EDGE,"E4");Q26=makeQuery(id+"F4.opChamfer","BLEND_EDGE",EDGE,{"blendedFrom":[makeQuery(id+"F3.opFillet","BLEND_EDGE",EDGE,{"blendedFrom":[makeQuery(id+"F1.opExtrude","SWEPT_EDGE",EDGE,{"disambiguationData":[OSD([subQ1,subQ0])]}),makeQuery(id+"F1.opExtrude","CAP_FACE",FACE,{"disambiguationData":[OSD([sQuery(id+"F0.wireOp",EDGE,"E0"),sQuery(id+"F0.wireOp",EDGE,"E1"),sQuery(id+"F0.wireOp",EDGE,"E2"),sQuery(id+"F0.wireOp",EDGE,"E3"),subQ1,subQ0,sQuery(id+"F0.wireOp",EDGE,"E6"),sQuery(id+"F0.wireOp",EDGE,"E7"),sQuery(id+"F0.wireOp",EDGE,"E8"),sQuery(id+"F0.wireOp",EDGE,"E9"),sQuery(id+"F0.wireOp",EDGE,"E10"),sQuery(id+"F0.wireOp",EDGE,"E11"),sQuery(id+"F0.wireOp",EDGE,"E12"),sQuery(id+"F0.wireOp",EDGE,"E13"),sQuery(id+"F0.wireOp",EDGE,"E14"),sQuery(id+"F0.wireOp",EDGE,"E15"),sQuery(id+"F0.wireOp",EDGE,"E16"),sQuery(id+"F0.wireOp",EDGE,"E17")])],"isStart":true})],"blendedInto":[makeQuery(id+"F1.opExtrude","CAP_FACE",FACE,{"disambiguationData":[OSD([sQuery(id+"F0.wireOp",EDGE,"E0"),sQuery(id+"F0.wireOp",EDGE,"E1"),sQuery(id+"F0.wireOp",EDGE,"E2"),sQuery(id+"F0.wireOp",EDGE,"E3"),subQ1,subQ0,sQuery(id+"F0.wireOp",EDGE,"E6"),sQuery(id+"F0.wireOp",EDGE,"E7"),sQuery(id+"F0.wireOp",EDGE,"E8"),sQuery(id+"F0.wireOp",EDGE,"E9"),sQuery(id+"F0.wireOp",EDGE,"E10"),sQuery(id+"F0.wireOp",EDGE,"E11"),sQuery(id+"F0.wireOp",EDGE,"E12"),sQuery(id+"F0.wireOp",EDGE,"E13"),sQuery(id+"F0.wireOp",EDGE,"E14"),sQuery(id+"F0.wireOp",EDGE,"E15"),sQuery(id+"F0.wireOp",EDGE,"E16"),sQuery(id+"F0.wireOp",EDGE,"E17")])],"isStart":true})]}),makeQuery(id+"F3.opFillet","BLEND_FACE",FACE,{"disambiguationData":[OSD([subQ1,subQ0])]})],"blendedInto":[makeQuery(id+"F3.opFillet","BLEND_FACE",FACE,{"disambiguationData":[OSD([subQ1,subQ0])]})]});}
            var Q27;
            {var subQ0=sQuery(id+"F0.wireOp",EDGE,"E5");Q27=makeQuery(id+"F4.opChamfer","BLEND_EDGE",EDGE,{"blendedFrom":[makeQuery(id+"F1.opExtrude","CAP_EDGE",EDGE,{"disambiguationData":[OSD([subQ0])],"isStart":true}),makeQuery(id+"F1.opExtrude","SWEPT_FACE",FACE,{"disambiguationData":[OSD([subQ0])]})],"blendedInto":[makeQuery(id+"F1.opExtrude","SWEPT_FACE",FACE,{"disambiguationData":[OSD([subQ0])]})]});}
            var Q28;
            {var subQ0=sQuery(id+"F0.wireOp",EDGE,"E12");var subQ1=sQuery(id+"F0.wireOp",EDGE,"E5");Q28=makeQuery(id+"F4.opChamfer","BLEND_EDGE",EDGE,{"blendedFrom":[makeQuery(id+"F3.opFillet","BLEND_EDGE",EDGE,{"blendedFrom":[makeQuery(id+"F1.opExtrude","SWEPT_EDGE",EDGE,{"disambiguationData":[OSD([subQ1,subQ0])]}),makeQuery(id+"F1.opExtrude","CAP_FACE",FACE,{"disambiguationData":[OSD([sQuery(id+"F0.wireOp",EDGE,"E0"),sQuery(id+"F0.wireOp",EDGE,"E1"),sQuery(id+"F0.wireOp",EDGE,"E2"),sQuery(id+"F0.wireOp",EDGE,"E3"),sQuery(id+"F0.wireOp",EDGE,"E4"),subQ1,sQuery(id+"F0.wireOp",EDGE,"E6"),sQuery(id+"F0.wireOp",EDGE,"E7"),sQuery(id+"F0.wireOp",EDGE,"E8"),sQuery(id+"F0.wireOp",EDGE,"E9"),sQuery(id+"F0.wireOp",EDGE,"E10"),sQuery(id+"F0.wireOp",EDGE,"E11"),subQ0,sQuery(id+"F0.wireOp",EDGE,"E13"),sQuery(id+"F0.wireOp",EDGE,"E14"),sQuery(id+"F0.wireOp",EDGE,"E15"),sQuery(id+"F0.wireOp",EDGE,"E16"),sQuery(id+"F0.wireOp",EDGE,"E17")])],"isStart":true})],"blendedInto":[makeQuery(id+"F1.opExtrude","CAP_FACE",FACE,{"disambiguationData":[OSD([sQuery(id+"F0.wireOp",EDGE,"E0"),sQuery(id+"F0.wireOp",EDGE,"E1"),sQuery(id+"F0.wireOp",EDGE,"E2"),sQuery(id+"F0.wireOp",EDGE,"E3"),sQuery(id+"F0.wireOp",EDGE,"E4"),subQ1,sQuery(id+"F0.wireOp",EDGE,"E6"),sQuery(id+"F0.wireOp",EDGE,"E7"),sQuery(id+"F0.wireOp",EDGE,"E8"),sQuery(id+"F0.wireOp",EDGE,"E9"),sQuery(id+"F0.wireOp",EDGE,"E10"),sQuery(id+"F0.wireOp",EDGE,"E11"),subQ0,sQuery(id+"F0.wireOp",EDGE,"E13"),sQuery(id+"F0.wireOp",EDGE,"E14"),sQuery(id+"F0.wireOp",EDGE,"E15"),sQuery(id+"F0.wireOp",EDGE,"E16"),sQuery(id+"F0.wireOp",EDGE,"E17")])],"isStart":true})]}),makeQuery(id+"F3.opFillet","BLEND_FACE",FACE,{"disambiguationData":[OSD([subQ1,subQ0])]})],"blendedInto":[makeQuery(id+"F3.opFillet","BLEND_FACE",FACE,{"disambiguationData":[OSD([subQ1,subQ0])]})]});}
            var Q29;
            {var subQ0=sQuery(id+"F0.wireOp",EDGE,"E12");Q29=makeQuery(id+"F4.opChamfer","BLEND_EDGE",EDGE,{"blendedFrom":[makeQuery(id+"F1.opExtrude","CAP_EDGE",EDGE,{"disambiguationData":[OSD([subQ0])],"isStart":true}),makeQuery(id+"F1.opExtrude","SWEPT_FACE",FACE,{"disambiguationData":[OSD([subQ0])]})],"blendedInto":[makeQuery(id+"F1.opExtrude","SWEPT_FACE",FACE,{"disambiguationData":[OSD([subQ0])]})]});}
            var Q30;
            {var subQ0=sQuery(id+"F0.wireOp",EDGE,"E12");var subQ1=sQuery(id+"F0.wireOp",EDGE,"E7");Q30=makeQuery(id+"F4.opChamfer","BLEND_EDGE",EDGE,{"blendedFrom":[makeQuery(id+"F3.opFillet","BLEND_EDGE",EDGE,{"blendedFrom":[makeQuery(id+"F2.opChamfer","BLEND_EDGE",EDGE,{"blendedFrom":[makeQuery(id+"F1.opExtrude","SWEPT_EDGE",EDGE,{"disambiguationData":[OSD([subQ1,subQ0])]}),makeQuery(id+"F1.opExtrude","SWEPT_FACE",FACE,{"disambiguationData":[OSD([subQ0])]})],"blendedInto":[makeQuery(id+"F1.opExtrude","SWEPT_FACE",FACE,{"disambiguationData":[OSD([subQ0])]})]}),makeQuery(id+"F1.opExtrude","CAP_FACE",FACE,{"disambiguationData":[OSD([sQuery(id+"F0.wireOp",EDGE,"E0"),sQuery(id+"F0.wireOp",EDGE,"E1"),sQuery(id+"F0.wireOp",EDGE,"E2"),sQuery(id+"F0.wireOp",EDGE,"E3"),sQuery(id+"F0.wireOp",EDGE,"E4"),sQuery(id+"F0.wireOp",EDGE,"E5"),sQuery(id+"F0.wireOp",EDGE,"E6"),subQ1,sQuery(id+"F0.wireOp",EDGE,"E8"),sQuery(id+"F0.wireOp",EDGE,"E9"),sQuery(id+"F0.wireOp",EDGE,"E10"),sQuery(id+"F0.wireOp",EDGE,"E11"),subQ0,sQuery(id+"F0.wireOp",EDGE,"E13"),sQuery(id+"F0.wireOp",EDGE,"E14"),sQuery(id+"F0.wireOp",EDGE,"E15"),sQuery(id+"F0.wireOp",EDGE,"E16"),sQuery(id+"F0.wireOp",EDGE,"E17")])],"isStart":true})],"blendedInto":[makeQuery(id+"F1.opExtrude","CAP_FACE",FACE,{"disambiguationData":[OSD([sQuery(id+"F0.wireOp",EDGE,"E0"),sQuery(id+"F0.wireOp",EDGE,"E1"),sQuery(id+"F0.wireOp",EDGE,"E2"),sQuery(id+"F0.wireOp",EDGE,"E3"),sQuery(id+"F0.wireOp",EDGE,"E4"),sQuery(id+"F0.wireOp",EDGE,"E5"),sQuery(id+"F0.wireOp",EDGE,"E6"),subQ1,sQuery(id+"F0.wireOp",EDGE,"E8"),sQuery(id+"F0.wireOp",EDGE,"E9"),sQuery(id+"F0.wireOp",EDGE,"E10"),sQuery(id+"F0.wireOp",EDGE,"E11"),subQ0,sQuery(id+"F0.wireOp",EDGE,"E13"),sQuery(id+"F0.wireOp",EDGE,"E14"),sQuery(id+"F0.wireOp",EDGE,"E15"),sQuery(id+"F0.wireOp",EDGE,"E16"),sQuery(id+"F0.wireOp",EDGE,"E17")])],"isStart":true})]}),makeQuery(id+"F3.opFillet","BLEND_FACE",FACE,{"disambiguationData":[OSD([subQ1,subQ0])]})],"blendedInto":[makeQuery(id+"F3.opFillet","BLEND_FACE",FACE,{"disambiguationData":[OSD([subQ1,subQ0])]})]});}
            var Q31;
            {var subQ0=sQuery(id+"F0.wireOp",EDGE,"E12");var subQ1=sQuery(id+"F0.wireOp",EDGE,"E7");Q31=makeQuery(id+"F4.opChamfer","BLEND_EDGE",EDGE,{"blendedFrom":[makeQuery(id+"F2.opChamfer","BLEND_EDGE",EDGE,{"blendedFrom":[makeQuery(id+"F1.opExtrude","SWEPT_EDGE",EDGE,{"disambiguationData":[OSD([subQ1,subQ0])]}),makeQuery(id+"F1.opExtrude","CAP_FACE",FACE,{"disambiguationData":[OSD([sQuery(id+"F0.wireOp",EDGE,"E0"),sQuery(id+"F0.wireOp",EDGE,"E1"),sQuery(id+"F0.wireOp",EDGE,"E2"),sQuery(id+"F0.wireOp",EDGE,"E3"),sQuery(id+"F0.wireOp",EDGE,"E4"),sQuery(id+"F0.wireOp",EDGE,"E5"),sQuery(id+"F0.wireOp",EDGE,"E6"),subQ1,sQuery(id+"F0.wireOp",EDGE,"E8"),sQuery(id+"F0.wireOp",EDGE,"E9"),sQuery(id+"F0.wireOp",EDGE,"E10"),sQuery(id+"F0.wireOp",EDGE,"E11"),subQ0,sQuery(id+"F0.wireOp",EDGE,"E13"),sQuery(id+"F0.wireOp",EDGE,"E14"),sQuery(id+"F0.wireOp",EDGE,"E15"),sQuery(id+"F0.wireOp",EDGE,"E16"),sQuery(id+"F0.wireOp",EDGE,"E17")])],"isStart":true})],"blendedInto":[makeQuery(id+"F1.opExtrude","CAP_FACE",FACE,{"disambiguationData":[OSD([sQuery(id+"F0.wireOp",EDGE,"E0"),sQuery(id+"F0.wireOp",EDGE,"E1"),sQuery(id+"F0.wireOp",EDGE,"E2"),sQuery(id+"F0.wireOp",EDGE,"E3"),sQuery(id+"F0.wireOp",EDGE,"E4"),sQuery(id+"F0.wireOp",EDGE,"E5"),sQuery(id+"F0.wireOp",EDGE,"E6"),subQ1,sQuery(id+"F0.wireOp",EDGE,"E8"),sQuery(id+"F0.wireOp",EDGE,"E9"),sQuery(id+"F0.wireOp",EDGE,"E10"),sQuery(id+"F0.wireOp",EDGE,"E11"),subQ0,sQuery(id+"F0.wireOp",EDGE,"E13"),sQuery(id+"F0.wireOp",EDGE,"E14"),sQuery(id+"F0.wireOp",EDGE,"E15"),sQuery(id+"F0.wireOp",EDGE,"E16"),sQuery(id+"F0.wireOp",EDGE,"E17")])],"isStart":true})]}),makeQuery(id+"F2.opChamfer","BLEND_FACE",FACE,{"disambiguationData":[OSD([subQ1,subQ0])]})],"blendedInto":[makeQuery(id+"F2.opChamfer","BLEND_FACE",FACE,{"disambiguationData":[OSD([subQ1,subQ0])]})]});}
            fillet(context, id + "F5", {"entities" : qUnion([Q0, Q1, Q2, Q3, Q4, Q5, Q6, Q7, Q8, Q9, Q10, Q11, Q12, Q13, Q14, Q15, Q16, Q17, Q18, Q19, Q20, Q21, Q22, Q23, Q24, Q25, Q26, Q27, Q28, Q29, Q30, Q31]), "radius" : 1 * mm, "tangentPropagation" : true, "allowEdgeOverflow" : false});
        }
        {
            var Q0;
            Q0=makeQuery(id+"F1.opExtrude","SWEPT_FACE",FACE,{"disambiguationData":[OSD([sQuery(id+"F0.wireOp",EDGE,"E15")])]});
            var sketch = newSketch(context, id + "F6", { "sketchPlane" : qUnion([Q0])});
            skLineSegment(sketch, "E18", {"start": v(-10, 13.7) * mm, "end": v(10, -6.3) * mm, "construction": true});
            skLineSegment(sketch, "E19", {"start": v(10, 13.7) * mm, "end": v(-10, -6.3) * mm, "construction": true});
            skLineSegment(sketch, "E20", {"start": v(-10, -6.3) * mm, "end": v(10, -6.3) * mm, "construction": true});
            skPoint(sketch, "E21", {"position": v(0, 3.7) * mm});
            skSolve(sketch);
        }
        {
            var Q0;
            Q0=sQuery(id+"F6.wireOp",VERTEX,"E21");
            var Q1;
            Q1=makeQuery(id+"F1.opExtrude","SWEPT_BODY",BODY,{"disambiguationData":[OSD([sQuery(id+"F0.wireOp",EDGE,"E0"),sQuery(id+"F0.wireOp",EDGE,"E1"),sQuery(id+"F0.wireOp",EDGE,"E2"),sQuery(id+"F0.wireOp",EDGE,"E3"),sQuery(id+"F0.wireOp",EDGE,"E4"),sQuery(id+"F0.wireOp",EDGE,"E5"),sQuery(id+"F0.wireOp",EDGE,"E6"),sQuery(id+"F0.wireOp",EDGE,"E7"),sQuery(id+"F0.wireOp",EDGE,"E8"),sQuery(id+"F0.wireOp",EDGE,"E9"),sQuery(id+"F0.wireOp",EDGE,"E10"),sQuery(id+"F0.wireOp",EDGE,"E11"),sQuery(id+"F0.wireOp",EDGE,"E12"),sQuery(id+"F0.wireOp",EDGE,"E13"),sQuery(id+"F0.wireOp",EDGE,"E14"),sQuery(id+"F0.wireOp",EDGE,"E15"),sQuery(id+"F0.wireOp",EDGE,"E16"),sQuery(id+"F0.wireOp",EDGE,"E17")])]});
            hole(context, id + "F7", {"style" : HoleStyle.C_SINK, "endStyle" : HoleEndStyle.BLIND, "holeDiameter" : 6.1 * mm, "cSinkDiameter" : 9 * mm, "cSinkAngle" : 90 * degree, "majorDiameter" : 5 * mm, "holeDepth" : 20 * mm, "isTappedThrough" : true, "tappedDepth" : 12 * mm, "tapClearance" : 3, "locations" : qUnion([Q0]), "scope" : qUnion([Q1])});
        }
    });
